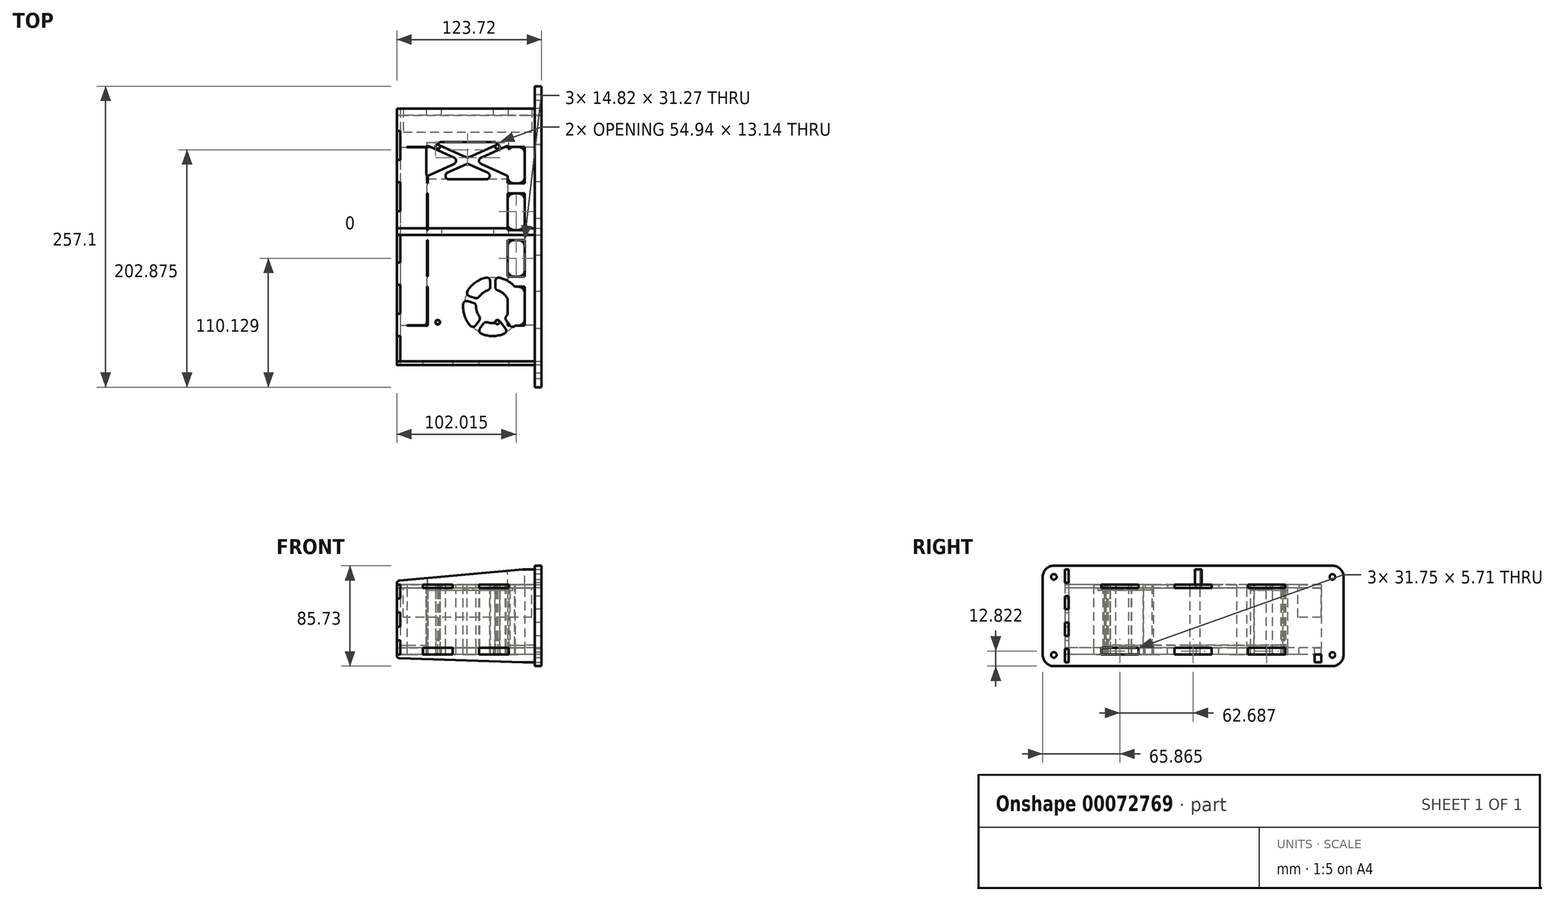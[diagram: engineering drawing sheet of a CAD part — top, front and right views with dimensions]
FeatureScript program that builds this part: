
annotation { "Feature Type Name" : "Feature", "Feature Type Description" : "" }
export const myFeature = defineFeature(function(context is Context, id is Id, definition is map)
    precondition{}
    {
        {
            assignVariable(context, id + "F0", {"name" : "duron_thin", "anyValue" : 3 * mm});
        }
        {
            assignVariable(context, id + "F1", {"name" : "duron_thick", "anyValue" : 5.7 * mm});
        }
        {
            var Q0;
            Q0=qCreatedBy(makeId("Top.planeOp"),FACE);
            var sketch = newSketch(context, id + "F2", { "sketchPlane" : qUnion([Q0])});
            skLineSegment(sketch, "E0.rect.bottom", {"start": v(57.5, 108) * mm, "end": v(-57.5, 108) * mm});
            skLineSegment(sketch, "E0.rect.top", {"start": v(57.5, -108) * mm, "end": v(-57.5, -108) * mm});
            skLineSegment(sketch, "E0.rect.left", {"start": v(57.5, 108) * mm, "end": v(57.5, -108) * mm});
            skLineSegment(sketch, "E0.rect.right", {"start": v(-57.5, 108) * mm, "end": v(-57.5, -108) * mm});
            skPoint(sketch, "E0.rect.middle", {"position": v(0, 0) * mm});
            skSolve(sketch);
        }
        {
            var Q0;
            Q0 = qSketchRegion(id + "F2", true);
            extrude(context, id + "F3", {"entities" : qUnion([Q0]), "depth" : 50 * mm + 1 * mm});
        }
        {
            var Q0;
            Q0=makeQuery(id+"F3.opExtrude","CAP_FACE",FACE,{"disambiguationData":[OSD([sQuery(id+"F2.wireOp",EDGE,"E0.rect.bottom"),sQuery(id+"F2.wireOp",EDGE,"E0.rect.top"),sQuery(id+"F2.wireOp",EDGE,"E0.rect.left"),sQuery(id+"F2.wireOp",EDGE,"E0.rect.right")])],"isStart":false});
            var sketch = newSketch(context, id + "F4", { "sketchPlane" : qUnion([Q0])});
            skCircle(sketch, "E1", {"center": v(21.5, -61) * mm, "radius": 24.5 * mm});
            skLineSegment(sketch, "E2.bottom", {"start": v(-55, 108) * mm, "end": v(55, 108) * mm});
            skLineSegment(sketch, "E2.top", {"start": v(-55, 88) * mm, "end": v(55, 88) * mm});
            skLineSegment(sketch, "E2.left", {"start": v(-55, 108) * mm, "end": v(-55, 88) * mm});
            skLineSegment(sketch, "E2.right", {"start": v(55, 108) * mm, "end": v(55, 88) * mm});
            skLineSegment(sketch, "E3.rect.bottom", {"start": v(-35, 79) * mm, "end": v(35, 79) * mm});
            skLineSegment(sketch, "E3.rect.top", {"start": v(-35, 48) * mm, "end": v(35, 48) * mm});
            skLineSegment(sketch, "E3.rect.left", {"start": v(-35, 79) * mm, "end": v(-35, 48) * mm});
            skLineSegment(sketch, "E3.rect.right", {"start": v(35, 79) * mm, "end": v(35, 48) * mm});
            skPoint(sketch, "E3.rect.middle", {"position": v(0, 63.5) * mm});
            skSolve(sketch);
        }
        {
            var Q0;
            Q0=makeQuery(id+"F4.imprint","IMPRINT",FACE,{"disambiguationData":[TD([[makeQuery(id+"F4.imprint","IMPRINT",EDGE,{"derivedFrom":sQuery(id+"F4.wireOp",EDGE,"E1")}),1.0]])]});
            var Q1;
            Q1=makeQuery(id+"F4.imprint","IMPRINT",FACE,{"disambiguationData":[TD([[makeQuery(id+"F4.imprint","IMPRINT",EDGE,{"derivedFrom":sQuery(id+"F4.wireOp",EDGE,"E3.rect.bottom")}),-1.0]])]});
            extrude(context, id + "F5", {"entities" : qUnion([Q0, Q1]), "operationType" : NewBodyOperationType.REMOVE, "oppositeDirection" : true, "depth" : 2 * mm});
        }
        {
            var Q0;
            Q0=makeQuery(id+"F4.imprint","IMPRINT",FACE,{"disambiguationData":[TD([[makeQuery(id+"F4.imprint","IMPRINT",EDGE,{"derivedFrom":sQuery(id+"F4.wireOp",EDGE,"E2.bottom")}),1.0]])]});
            extrude(context, id + "F6", {"entities" : qUnion([Q0]), "operationType" : NewBodyOperationType.REMOVE, "oppositeDirection" : true, "depth" : 25 * mm});
        }
        {
            var Q0;
            Q0=makeQuery(id+"F3.opExtrude","CAP_FACE",FACE,{"disambiguationData":[OSD([sQuery(id+"F2.wireOp",EDGE,"E0.rect.bottom"),sQuery(id+"F2.wireOp",EDGE,"E0.rect.top"),sQuery(id+"F2.wireOp",EDGE,"E0.rect.left"),sQuery(id+"F2.wireOp",EDGE,"E0.rect.right")])],"isStart":true});
            var sketch = newSketch(context, id + "F7", { "sketchPlane" : qUnion([Q0])});
            skLineSegment(sketch, "E4.bottom", {"start": v(57.5, 77) * mm, "end": v(34.5, 77) * mm});
            skLineSegment(sketch, "E4.top", {"start": v(57.5, -75) * mm, "end": v(34.5, -75) * mm});
            skLineSegment(sketch, "E4.left", {"start": v(57.5, 77) * mm, "end": v(57.5, -75) * mm});
            skLineSegment(sketch, "E4.right", {"start": v(34.5, 77) * mm, "end": v(34.5, -75) * mm});
            skLineSegment(sketch, "E5.bottom", {"start": v(-57.5, 77) * mm, "end": v(-34.5, 77) * mm});
            skLineSegment(sketch, "E5.top", {"start": v(-57.5, -75) * mm, "end": v(-34.5, -75) * mm});
            skLineSegment(sketch, "E5.left", {"start": v(-57.5, 77) * mm, "end": v(-57.5, -75) * mm});
            skLineSegment(sketch, "E5.right", {"start": v(-34.5, 77) * mm, "end": v(-34.5, -75) * mm});
            skPoint(sketch, "E6", {"position": v(48.25, -80) * mm});
            skPoint(sketch, "E7", {"position": v(48.25, 98.75) * mm});
            skPoint(sketch, "E8", {"position": v(-48.25, 98.75) * mm});
            skPoint(sketch, "E9", {"position": v(-48.25, -80) * mm});
            skPoint(sketch, "E10", {"position": v(-8, 10) * mm});
            skPoint(sketch, "E11", {"position": v(25.5, 74.5) * mm});
            skPoint(sketch, "E12", {"position": v(-25.5, 74.5) * mm});
            skPoint(sketch, "E13", {"position": v(25.5, -75.5) * mm});
            skPoint(sketch, "E14", {"position": v(-25.5, -75.5) * mm});
            skSolve(sketch);
        }
        {
            var Q0;
            Q0=makeQuery(id+"F7.imprint","IMPRINT",FACE,{"disambiguationData":[TD([[makeQuery(id+"F7.imprint","IMPRINT",EDGE,{"derivedFrom":sQuery(id+"F7.wireOp",EDGE,"E4.bottom")}),1.0]])]});
            var Q1;
            Q1=makeQuery(id+"F7.imprint","IMPRINT",FACE,{"disambiguationData":[TD([[makeQuery(id+"F7.imprint","IMPRINT",EDGE,{"derivedFrom":sQuery(id+"F7.wireOp",EDGE,"E5.bottom")}),-1.0]])]});
            extrude(context, id + "F8", {"entities" : qUnion([Q0, Q1]), "operationType" : NewBodyOperationType.REMOVE, "oppositeDirection" : true, "depth" : 2 * mm});
        }
        {
            var Q0;
            Q0=sQuery(id+"F7.wireOp",VERTEX,"E11");
            var Q1;
            Q1=sQuery(id+"F7.wireOp",VERTEX,"E12");
            var Q2;
            Q2=sQuery(id+"F7.wireOp",VERTEX,"E13");
            var Q3;
            Q3=sQuery(id+"F7.wireOp",VERTEX,"E14");
            var Q4;
            Q4=makeQuery(id+"F3.opExtrude","SWEPT_BODY",BODY,{"disambiguationData":[OSD([sQuery(id+"F2.wireOp",EDGE,"E0.rect.bottom"),sQuery(id+"F2.wireOp",EDGE,"E0.rect.top"),sQuery(id+"F2.wireOp",EDGE,"E0.rect.left"),sQuery(id+"F2.wireOp",EDGE,"E0.rect.right")])]});
            hole(context, id + "F9", {"style" : HoleStyle.SIMPLE, "holeDiameter" : 3.5 * mm, "endStyle" : HoleEndStyle.BLIND, "holeDepth" : 6.35 * mm, "locations" : qUnion([Q0, Q1, Q2, Q3]), "scope" : qUnion([Q4])});
        }
        {
            var Q0;
            Q0=makeQuery(id+"F3.opExtrude","SWEPT_FACE",FACE,{"disambiguationData":[OSD([sQuery(id+"F2.wireOp",EDGE,"E0.rect.left")])]});
            var sketch = newSketch(context, id + "F10", { "sketchPlane" : qUnion([Q0])});
            skLineSegment(sketch, "E15.bottom", {"start": v(-130.05, 70.05) * mm, "end": v(127.05, 70.05) * mm});
            skLineSegment(sketch, "E15.top", {"start": v(-130.05, -15.67) * mm, "end": v(127.05, -15.67) * mm});
            skLineSegment(sketch, "E15.left", {"start": v(-130.05, 70.05) * mm, "end": v(-130.05, -15.68) * mm});
            skLineSegment(sketch, "E15.right", {"start": v(127.05, 70.05) * mm, "end": v(127.05, -15.67) * mm});
            skSolve(sketch);
        }
        {
            var Q0;
            Q0 = qSketchRegion(id + "F10", true);
            extrude(context, id + "F11", {"entities" : qUnion([Q0]), "depth" : getVariable(context, 'duron_thick')});
        }
        {
            var Q0;
            Q0=makeQuery(id+"F3.opExtrude","SWEPT_FACE",FACE,{"disambiguationData":[OSD([sQuery(id+"F2.wireOp",EDGE,"E0.rect.top")])]});
            var sketch = newSketch(context, id + "F12", { "sketchPlane" : qUnion([Q0])});
            skLineSegment(sketch, "E16.0.1", {"start": v(57.5, -15.68) * mm, "end": v(63.21, -15.68) * mm, "construction": true});
            skLineSegment(sketch, "E16.0.2", {"start": v(63.21, -12.5) * mm, "end": v(63.21, 66.88) * mm});
            skLineSegment(sketch, "E16.0.3", {"start": v(63.21, 70.05) * mm, "end": v(57.5, 70.05) * mm, "construction": true});
            skLineSegment(sketch, "E17.0.0", {"start": v(-57.5, 0) * mm, "end": v(57.5, 0) * mm, "construction": true});
            skLineSegment(sketch, "E17.0.2", {"start": v(57.5, 51) * mm, "end": v(-57.5, 51) * mm, "construction": true});
            skLineSegment(sketch, "E17.0.3", {"start": v(-57.5, 51) * mm, "end": v(-57.5, 0) * mm, "construction": true});
            skLineSegment(sketch, "E18", {"start": v(-60.5, 57.17) * mm, "end": v(-60.5, -8.89) * mm});
            skLineSegment(sketch, "E19", {"start": v(47.34, 66.88) * mm, "end": v(-60.5, 57.17) * mm});
            skLineSegment(sketch, "E20", {"start": v(-60.5, -8.9) * mm, "end": v(47.34, -12.5) * mm});
            skLineSegment(sketch, "E21", {"start": v(47.34, -12.5) * mm, "end": v(63.21, -12.5) * mm});
            skLineSegment(sketch, "E22", {"start": v(47.34, 66.88) * mm, "end": v(63.21, 66.88) * mm});
            skLineSegment(sketch, "E23.bottom", {"start": v(63.21, 55.54) * mm, "end": v(57.5, 55.54) * mm});
            skLineSegment(sketch, "E23.top", {"start": v(63.21, 44.2) * mm, "end": v(57.5, 44.2) * mm});
            skLineSegment(sketch, "E23.left", {"start": v(63.21, 55.54) * mm, "end": v(63.21, 44.2) * mm});
            skLineSegment(sketch, "E23.right", {"start": v(57.5, 55.54) * mm, "end": v(57.5, 44.2) * mm});
            skLineSegment(sketch, "E24.bottom", {"start": v(63.21, 32.86) * mm, "end": v(57.5, 32.86) * mm});
            skLineSegment(sketch, "E24.top", {"start": v(63.21, 21.52) * mm, "end": v(57.5, 21.52) * mm});
            skLineSegment(sketch, "E24.left", {"start": v(63.21, 32.86) * mm, "end": v(63.21, 21.52) * mm});
            skLineSegment(sketch, "E24.right", {"start": v(57.5, 32.86) * mm, "end": v(57.5, 21.52) * mm});
            skLineSegment(sketch, "E25.bottom", {"start": v(63.21, 10.18) * mm, "end": v(57.5, 10.18) * mm});
            skLineSegment(sketch, "E25.top", {"start": v(63.21, -1.16) * mm, "end": v(57.5, -1.16) * mm});
            skLineSegment(sketch, "E25.left", {"start": v(63.21, 10.18) * mm, "end": v(63.21, -1.16) * mm});
            skLineSegment(sketch, "E25.right", {"start": v(57.5, 10.18) * mm, "end": v(57.5, -1.16) * mm});
            skLineSegment(sketch, "E26", {"start": v(57.5, 44.2) * mm, "end": v(57.5, 32.86) * mm, "construction": true});
            skLineSegment(sketch, "E27", {"start": v(57.5, 21.52) * mm, "end": v(57.5, 10.18) * mm, "construction": true});
            skLineSegment(sketch, "E28", {"start": v(57.5, -1.16) * mm, "end": v(57.5, -12.5) * mm, "construction": true});
            skLineSegment(sketch, "E29", {"start": v(57.5, 55.54) * mm, "end": v(57.5, 66.88) * mm, "construction": true});
            skSolve(sketch);
        }
        {
            var Q0;
            Q0=makeQuery(id+"F12.imprint","IMPRINT",FACE,{"disambiguationData":[TD([[makeQuery(id+"F12.imprint","IMPRINT",EDGE,{"derivedFrom":sQuery(id+"F12.wireOp",EDGE,"E18")}),1.0]])]});
            var Q1;
            {var subQ6=sQuery(id+"F12.wireOp",EDGE,"E24.right");Q1=makeQuery(id+"F12.imprint","IMPRINT",FACE,{"disambiguationData":[TD([[makeQuery(id+"F12.imprint","IMPRINT",EDGE,{"derivedFrom":subQ6}),-1.0]])]});}
            var Q2;
            {var subQ0=sQuery(id+"F12.wireOp",EDGE,"E23.top");Q2=makeQuery(id+"F12.imprint","IMPRINT",FACE,{"disambiguationData":[TD([[makeQuery(id+"F12.imprint","IMPRINT",EDGE,{"derivedFrom":subQ0}),1.0]])]});}
            var Q3;
            {var subQ0=sQuery(id+"F12.wireOp",EDGE,"E24.top");Q3=makeQuery(id+"F12.imprint","IMPRINT",FACE,{"disambiguationData":[TD([[makeQuery(id+"F12.imprint","IMPRINT",EDGE,{"derivedFrom":subQ0}),1.0]])]});}
            extrude(context, id + "F13", {"entities" : qUnion([Q0, Q1, Q2, Q3]), "depth" : getVariable(context, 'duron_thin')});
        }
        {
            var Q0;
            Q0=makeQuery(id+"F3.opExtrude","CAP_FACE",FACE,{"disambiguationData":[OSD([sQuery(id+"F2.wireOp",EDGE,"E0.rect.bottom"),sQuery(id+"F2.wireOp",EDGE,"E0.rect.top"),sQuery(id+"F2.wireOp",EDGE,"E0.rect.left"),sQuery(id+"F2.wireOp",EDGE,"E0.rect.right")])],"isStart":true});
            var sketch = newSketch(context, id + "F14", { "sketchPlane" : qUnion([Q0])});
            skLineSegment(sketch, "E30.bottom", {"start": v(63.22, -108) * mm, "end": v(57.5, -108) * mm, "construction": true});
            skLineSegment(sketch, "E30.top", {"start": v(63.21, 111) * mm, "end": v(57.5, 111) * mm});
            skLineSegment(sketch, "E30.left", {"start": v(63.22, -77.06) * mm, "end": v(63.22, -45.31) * mm});
            skLineSegment(sketch, "E30.right", {"start": v(-60.5, -108) * mm, "end": v(-60.5, 111) * mm});
            skLineSegment(sketch, "E31.bottom", {"start": v(63.21, 80.06) * mm, "end": v(57.5, 80.06) * mm});
            skLineSegment(sketch, "E31.top", {"start": v(63.21, 48.31) * mm, "end": v(57.5, 48.31) * mm});
            skLineSegment(sketch, "E31.left", {"start": v(63.21, 80.06) * mm, "end": v(63.21, 48.31) * mm});
            skLineSegment(sketch, "E31.right", {"start": v(57.5, 80.06) * mm, "end": v(57.5, 48.31) * mm, "construction": true});
            skLineSegment(sketch, "E32.bottom", {"start": v(63.21, 17.37) * mm, "end": v(57.5, 17.37) * mm});
            skLineSegment(sketch, "E32.top", {"start": v(63.21, -14.38) * mm, "end": v(57.5, -14.38) * mm});
            skLineSegment(sketch, "E32.left", {"start": v(63.21, 17.37) * mm, "end": v(63.21, -14.38) * mm});
            skLineSegment(sketch, "E32.right", {"start": v(57.5, 17.37) * mm, "end": v(57.5, -14.38) * mm, "construction": true});
            skLineSegment(sketch, "E33.bottom", {"start": v(63.21, -45.31) * mm, "end": v(57.5, -45.31) * mm});
            skLineSegment(sketch, "E33.top", {"start": v(63.21, -77.06) * mm, "end": v(57.5, -77.06) * mm});
            skLineSegment(sketch, "E33.left", {"start": v(63.21, -45.31) * mm, "end": v(63.21, -77.06) * mm});
            skLineSegment(sketch, "E33.right", {"start": v(57.5, -45.31) * mm, "end": v(57.5, -77.06) * mm, "construction": true});
            skLineSegment(sketch, "E34", {"start": v(57.5, -45.31) * mm, "end": v(57.5, -14.38) * mm});
            skLineSegment(sketch, "E35", {"start": v(57.5, 17.37) * mm, "end": v(57.5, 48.31) * mm});
            skLineSegment(sketch, "E36", {"start": v(57.5, 80.06) * mm, "end": v(57.5, 111) * mm});
            skLineSegment(sketch, "E37", {"start": v(57.5, -77.06) * mm, "end": v(57.5, -108) * mm});
            skLineSegment(sketch, "E38.trimOffspring", {"start": v(63.21, -14.38) * mm, "end": v(63.21, 17.37) * mm});
            skLineSegment(sketch, "E39.trimOffspring", {"start": v(63.21, 48.31) * mm, "end": v(63.21, 80.06) * mm});
            skLineSegment(sketch, "E40.top", {"start": v(35.1, 111) * mm, "end": v(9.7, 111) * mm});
            skLineSegment(sketch, "E40.left", {"start": v(35.1, 108) * mm, "end": v(35.1, 111) * mm});
            skLineSegment(sketch, "E40.right", {"start": v(9.7, 108) * mm, "end": v(9.7, 111) * mm});
            skLineSegment(sketch, "E41.top", {"start": v(-12.7, 111) * mm, "end": v(-38.1, 111) * mm});
            skLineSegment(sketch, "E41.left", {"start": v(-12.7, 108) * mm, "end": v(-12.7, 111) * mm});
            skLineSegment(sketch, "E41.right", {"start": v(-38.1, 108) * mm, "end": v(-38.1, 111) * mm});
            skLineSegment(sketch, "E42", {"start": v(9.7, 111) * mm, "end": v(-12.7, 111) * mm, "construction": true});
            skLineSegment(sketch, "E43", {"start": v(-38.1, 111) * mm, "end": v(-60.5, 111) * mm, "construction": true});
            skLineSegment(sketch, "E44", {"start": v(35.1, 111) * mm, "end": v(57.5, 111) * mm, "construction": true});
            skLineSegment(sketch, "E45", {"start": v(-38.1, 108) * mm, "end": v(-60.5, 108) * mm});
            skLineSegment(sketch, "E46", {"start": v(-12.7, 108) * mm, "end": v(9.7, 108) * mm});
            skLineSegment(sketch, "E47", {"start": v(35.1, 108) * mm, "end": v(57.5, 108) * mm});
            skLineSegment(sketch, "E48", {"start": v(57.5, -108) * mm, "end": v(-60.5, -108) * mm});
            skSolve(sketch);
        }
        {
            var Q0;
            {var subQ0=sQuery(id+"F7.wireOp",EDGE,"E5.bottom");Q0=makeQuery(id+"F14.imprint","IMPRINT",FACE,{"disambiguationData":[TD([[makeQuery(id+"F14.imprint","IMPRINT",EDGE,{"derivedFrom":makeQuery(id+"F8.boolean.opBoolean","COPY",EDGE,{"derivedFrom":makeQuery(id+"F8.opExtrude","CAP_EDGE",EDGE,{"disambiguationData":[OSD([subQ0])],"isStart":true})})}),-1.0]])]});}
            var Q1;
            {var subQ11=sQuery(id+"F14.wireOp",EDGE,"E37");Q1=makeQuery(id+"F14.imprint","IMPRINT",FACE,{"disambiguationData":[TD([[makeQuery(id+"F14.imprint","IMPRINT",EDGE,{"derivedFrom":subQ11}),1.0]])]});}
            var Q2;
            {var subQ0=sQuery(id+"F14.wireOp",EDGE,"E40.left");Q2=makeQuery(id+"F14.imprint","IMPRINT",FACE,{"disambiguationData":[TD([[makeQuery(id+"F14.imprint","IMPRINT",EDGE,{"derivedFrom":subQ0}),1.0]])]});}
            var Q3;
            {var subQ0=sQuery(id+"F14.wireOp",EDGE,"E41.left");Q3=makeQuery(id+"F14.imprint","IMPRINT",FACE,{"disambiguationData":[TD([[makeQuery(id+"F14.imprint","IMPRINT",EDGE,{"derivedFrom":subQ0}),1.0]])]});}
            var Q4;
            Q4=makeQuery(id+"F14.imprint","IMPRINT",FACE,{"disambiguationData":[TD([[makeQuery(id+"F14.imprint","IMPRINT",EDGE,{"derivedFrom":makeQuery(id+"F9.hole-1.boolean.opBoolean","COPY",EDGE,{"derivedFrom":makeQuery(id+"F9.hole-1.opRevolve","SWEPT_EDGE",EDGE,{"disambiguationData":[OSD([sQuery(id+"F9.hole-1.sketch.wireOp",EDGE,"core_line_2"),sQuery(id+"F9.hole-1.sketch.wireOp",EDGE,"core_line_3")])]})})}),1.0]])]});
            var Q5;
            Q5=makeQuery(id+"F14.imprint","IMPRINT",FACE,{"disambiguationData":[TD([[makeQuery(id+"F14.imprint","IMPRINT",EDGE,{"derivedFrom":makeQuery(id+"F9.hole-3.boolean.opBoolean","COPY",EDGE,{"derivedFrom":makeQuery(id+"F9.hole-3.opRevolve","SWEPT_EDGE",EDGE,{"disambiguationData":[OSD([sQuery(id+"F9.hole-3.sketch.wireOp",EDGE,"core_line_2"),sQuery(id+"F9.hole-3.sketch.wireOp",EDGE,"core_line_3")])]})})}),1.0]])]});
            var Q6;
            Q6=makeQuery(id+"F14.imprint","IMPRINT",FACE,{"disambiguationData":[TD([[makeQuery(id+"F14.imprint","IMPRINT",EDGE,{"derivedFrom":makeQuery(id+"F9.hole-0.boolean.opBoolean","COPY",EDGE,{"derivedFrom":makeQuery(id+"F9.hole-0.opRevolve","SWEPT_EDGE",EDGE,{"disambiguationData":[OSD([sQuery(id+"F9.hole-0.sketch.wireOp",EDGE,"core_line_2"),sQuery(id+"F9.hole-0.sketch.wireOp",EDGE,"core_line_3")])]})})}),1.0]])]});
            var Q7;
            Q7=makeQuery(id+"F14.imprint","IMPRINT",FACE,{"disambiguationData":[TD([[makeQuery(id+"F14.imprint","IMPRINT",EDGE,{"derivedFrom":makeQuery(id+"F9.hole-2.boolean.opBoolean","COPY",EDGE,{"derivedFrom":makeQuery(id+"F9.hole-2.opRevolve","SWEPT_EDGE",EDGE,{"disambiguationData":[OSD([sQuery(id+"F9.hole-2.sketch.wireOp",EDGE,"core_line_2"),sQuery(id+"F9.hole-2.sketch.wireOp",EDGE,"core_line_3")])]})})}),1.0]])]});
            var Q8;
            {var subQ10=sQuery(id+"F14.wireOp",EDGE,"E31.bottom");Q8=makeQuery(id+"F14.imprint","IMPRINT",FACE,{"disambiguationData":[TD([[makeQuery(id+"F14.imprint","IMPRINT",EDGE,{"derivedFrom":subQ10}),1.0]])]});}
            extrude(context, id + "F15", {"entities" : qUnion([Q0, Q1, Q2, Q3, Q4, Q5, Q6, Q7, Q8]), "depth" : getVariable(context, 'duron_thick')});
        }
        {
            var Q0;
            Q0=makeQuery(id+"F3.opExtrude","CAP_FACE",FACE,{"disambiguationData":[OSD([sQuery(id+"F2.wireOp",EDGE,"E0.rect.bottom"),sQuery(id+"F2.wireOp",EDGE,"E0.rect.top"),sQuery(id+"F2.wireOp",EDGE,"E0.rect.left"),sQuery(id+"F2.wireOp",EDGE,"E0.rect.right")])],"isStart":false});
            var sketch = newSketch(context, id + "F16", { "sketchPlane" : qUnion([Q0])});
            skLineSegment(sketch, "E49.0.0", {"start": v(-60.5, 108) * mm, "end": v(57.5, 108) * mm});
            skLineSegment(sketch, "E49.0.1", {"start": v(57.5, 108) * mm, "end": v(57.5, 77.06) * mm});
            skLineSegment(sketch, "E49.0.2", {"start": v(57.5, 77.06) * mm, "end": v(63.21, 77.06) * mm});
            skLineSegment(sketch, "E49.0.3", {"start": v(63.21, 77.06) * mm, "end": v(63.21, 45.31) * mm});
            skLineSegment(sketch, "E49.0.4", {"start": v(63.21, 45.31) * mm, "end": v(57.5, 45.31) * mm});
            skLineSegment(sketch, "E49.0.5", {"start": v(57.5, 45.31) * mm, "end": v(57.5, 14.38) * mm});
            skLineSegment(sketch, "E49.0.6", {"start": v(57.5, 14.38) * mm, "end": v(63.21, 14.38) * mm});
            skLineSegment(sketch, "E49.0.7", {"start": v(63.21, 14.38) * mm, "end": v(63.21, -17.37) * mm});
            skLineSegment(sketch, "E49.0.8", {"start": v(63.21, -17.37) * mm, "end": v(57.5, -17.37) * mm});
            skLineSegment(sketch, "E49.0.9", {"start": v(57.5, -17.37) * mm, "end": v(57.5, -48.31) * mm});
            skLineSegment(sketch, "E49.0.10", {"start": v(57.5, -48.31) * mm, "end": v(63.21, -48.31) * mm});
            skLineSegment(sketch, "E49.0.11", {"start": v(63.21, -48.31) * mm, "end": v(63.21, -80.06) * mm});
            skLineSegment(sketch, "E49.0.12", {"start": v(63.21, -80.06) * mm, "end": v(57.5, -80.06) * mm});
            skLineSegment(sketch, "E49.0.13", {"start": v(57.5, -80.06) * mm, "end": v(57.5, -108) * mm});
            skLineSegment(sketch, "E49.0.14", {"start": v(57.5, -108) * mm, "end": v(35.1, -108) * mm});
            skLineSegment(sketch, "E49.0.15", {"start": v(35.1, -108) * mm, "end": v(35.1, -111) * mm});
            skLineSegment(sketch, "E49.0.16", {"start": v(35.1, -111) * mm, "end": v(9.7, -111) * mm});
            skLineSegment(sketch, "E49.0.17", {"start": v(9.7, -111) * mm, "end": v(9.7, -108) * mm});
            skLineSegment(sketch, "E49.0.18", {"start": v(9.7, -108) * mm, "end": v(-12.7, -108) * mm});
            skLineSegment(sketch, "E49.0.19", {"start": v(-12.7, -108) * mm, "end": v(-12.7, -111) * mm});
            skLineSegment(sketch, "E49.0.20", {"start": v(-12.7, -111) * mm, "end": v(-38.1, -111) * mm});
            skLineSegment(sketch, "E49.0.21", {"start": v(-38.1, -111) * mm, "end": v(-38.1, -108) * mm});
            skLineSegment(sketch, "E49.0.22", {"start": v(-38.1, -108) * mm, "end": v(-60.5, -108) * mm});
            skLineSegment(sketch, "E49.0.23", {"start": v(-60.5, -108) * mm, "end": v(-60.5, 108) * mm});
            skSolve(sketch);
        }
        {
            var Q0;
            Q0 = qSketchRegion(id + "F16", true);
            extrude(context, id + "F17", {"entities" : qUnion([Q0]), "depth" : getVariable(context, 'duron_thin')});
        }
        {
            var Q0;
            Q0=makeQuery(id+"F3.opExtrude","SWEPT_FACE",FACE,{"disambiguationData":[OSD([sQuery(id+"F2.wireOp",EDGE,"E0.rect.right")])]});
            var sketch = newSketch(context, id + "F18", { "sketchPlane" : qUnion([Q0])});
            skLineSegment(sketch, "E50.bottom", {"start": v(-88.95, 54) * mm, "end": v(-64.2, 54) * mm});
            skLineSegment(sketch, "E50.top", {"start": v(-88.95, -5.72) * mm, "end": v(-64.2, -5.72) * mm});
            skLineSegment(sketch, "E50.left", {"start": v(-108, 54) * mm, "end": v(-108, -5.72) * mm});
            skLineSegment(sketch, "E50.right", {"start": v(111, 54) * mm, "end": v(111, 42.05) * mm});
            skLineSegment(sketch, "E51.bottom", {"start": v(111, 42.05) * mm, "end": v(108, 42.05) * mm});
            skLineSegment(sketch, "E51.top", {"start": v(111, 30.11) * mm, "end": v(108, 30.11) * mm});
            skLineSegment(sketch, "E51.right", {"start": v(108, 42.05) * mm, "end": v(108, 30.11) * mm});
            skLineSegment(sketch, "E52.bottom", {"start": v(111, 18.17) * mm, "end": v(108, 18.17) * mm});
            skLineSegment(sketch, "E52.top", {"start": v(111, 6.23) * mm, "end": v(108, 6.23) * mm});
            skLineSegment(sketch, "E52.right", {"start": v(108, 18.17) * mm, "end": v(108, 6.23) * mm});
            skLineSegment(sketch, "E53", {"start": v(108, 18.17) * mm, "end": v(108, 30.11) * mm, "construction": true});
            skLineSegment(sketch, "E54", {"start": v(108, 42.05) * mm, "end": v(108, 54) * mm, "construction": true});
            skLineSegment(sketch, "E55", {"start": v(108, 6.23) * mm, "end": v(108, -5.72) * mm, "construction": true});
            skLineSegment(sketch, "E56.trimOffspring", {"start": v(111, 30.11) * mm, "end": v(111, 18.17) * mm});
            skLineSegment(sketch, "E57.trimOffspring", {"start": v(111, 6.23) * mm, "end": v(111, -5.72) * mm});
            skLineSegment(sketch, "E58.top", {"start": v(-108, 51) * mm, "end": v(-88.95, 51) * mm});
            skLineSegment(sketch, "E58.left", {"start": v(-108, 54) * mm, "end": v(-108, 51) * mm});
            skLineSegment(sketch, "E58.right", {"start": v(-88.95, 54) * mm, "end": v(-88.95, 51) * mm});
            skLineSegment(sketch, "E59.top", {"start": v(-64.2, 51) * mm, "end": v(-45.15, 51) * mm});
            skLineSegment(sketch, "E59.left", {"start": v(-64.2, 54) * mm, "end": v(-64.2, 51) * mm});
            skLineSegment(sketch, "E59.right", {"start": v(-45.15, 54) * mm, "end": v(-45.15, 51) * mm});
            skLineSegment(sketch, "E60.top", {"start": v(-20.4, 51) * mm, "end": v(-1.35, 51) * mm});
            skLineSegment(sketch, "E60.left", {"start": v(-20.4, 54) * mm, "end": v(-20.4, 51) * mm});
            skLineSegment(sketch, "E60.right", {"start": v(-1.35, 54) * mm, "end": v(-1.35, 51) * mm});
            skLineSegment(sketch, "E61.top", {"start": v(23.4, 51) * mm, "end": v(42.45, 51) * mm});
            skLineSegment(sketch, "E61.left", {"start": v(23.4, 54) * mm, "end": v(23.4, 51) * mm});
            skLineSegment(sketch, "E61.right", {"start": v(42.45, 54) * mm, "end": v(42.45, 51) * mm});
            skLineSegment(sketch, "E62.top", {"start": v(67.2, 51) * mm, "end": v(86.25, 51) * mm});
            skLineSegment(sketch, "E62.left", {"start": v(67.2, 54) * mm, "end": v(67.2, 51) * mm});
            skLineSegment(sketch, "E62.right", {"start": v(86.25, 54) * mm, "end": v(86.25, 51) * mm});
            skLineSegment(sketch, "E63.top", {"start": v(-108, 0) * mm, "end": v(-88.95, 0) * mm});
            skLineSegment(sketch, "E63.left", {"start": v(-108, -5.72) * mm, "end": v(-108, 0) * mm});
            skLineSegment(sketch, "E63.right", {"start": v(-88.95, -5.72) * mm, "end": v(-88.95, 0) * mm});
            skLineSegment(sketch, "E64.top", {"start": v(-64.2, 0) * mm, "end": v(-45.15, 0) * mm});
            skLineSegment(sketch, "E64.left", {"start": v(-64.2, -5.72) * mm, "end": v(-64.2, 0) * mm});
            skLineSegment(sketch, "E64.right", {"start": v(-45.15, -5.72) * mm, "end": v(-45.15, 0) * mm});
            skLineSegment(sketch, "E65.top", {"start": v(-20.4, 0) * mm, "end": v(-1.35, 0) * mm});
            skLineSegment(sketch, "E65.left", {"start": v(-20.4, -5.72) * mm, "end": v(-20.4, 0) * mm});
            skLineSegment(sketch, "E65.right", {"start": v(-1.35, -5.72) * mm, "end": v(-1.35, 0) * mm});
            skLineSegment(sketch, "E66.top", {"start": v(23.4, 0) * mm, "end": v(42.45, 0) * mm});
            skLineSegment(sketch, "E66.left", {"start": v(23.4, -5.71) * mm, "end": v(23.4, 0) * mm});
            skLineSegment(sketch, "E66.right", {"start": v(42.45, -5.71) * mm, "end": v(42.45, 0) * mm});
            skLineSegment(sketch, "E67.top", {"start": v(67.2, 0) * mm, "end": v(86.25, 0) * mm});
            skLineSegment(sketch, "E67.left", {"start": v(67.2, -5.71) * mm, "end": v(67.2, 0) * mm});
            skLineSegment(sketch, "E67.right", {"start": v(86.25, -5.71) * mm, "end": v(86.25, 0) * mm});
            skLineSegment(sketch, "E68", {"start": v(-88.95, 51) * mm, "end": v(-64.2, 51) * mm, "construction": true});
            skLineSegment(sketch, "E69", {"start": v(-45.15, 51) * mm, "end": v(-20.4, 51) * mm, "construction": true});
            skLineSegment(sketch, "E70", {"start": v(-1.35, 51) * mm, "end": v(23.4, 51) * mm, "construction": true});
            skLineSegment(sketch, "E71", {"start": v(42.45, 51) * mm, "end": v(67.2, 51) * mm, "construction": true});
            skLineSegment(sketch, "E72", {"start": v(86.25, 51) * mm, "end": v(111, 51) * mm, "construction": true});
            skLineSegment(sketch, "E73.trimOffspring", {"start": v(-45.15, 54) * mm, "end": v(-20.4, 54) * mm});
            skLineSegment(sketch, "E74.trimOffspring", {"start": v(-1.35, 54) * mm, "end": v(23.4, 54) * mm});
            skLineSegment(sketch, "E75.trimOffspring", {"start": v(42.45, 54) * mm, "end": v(67.2, 54) * mm});
            skLineSegment(sketch, "E76.trimOffspring", {"start": v(86.25, 54) * mm, "end": v(111, 54) * mm});
            skLineSegment(sketch, "E77.trimOffspring", {"start": v(86.25, -5.72) * mm, "end": v(111, -5.72) * mm});
            skLineSegment(sketch, "E78.trimOffspring", {"start": v(42.45, -5.72) * mm, "end": v(67.2, -5.72) * mm});
            skLineSegment(sketch, "E79.trimOffspring", {"start": v(-1.35, -5.72) * mm, "end": v(23.4, -5.72) * mm});
            skLineSegment(sketch, "E80.trimOffspring", {"start": v(-45.15, -5.72) * mm, "end": v(-20.4, -5.72) * mm});
            skSolve(sketch);
        }
        {
            var Q0;
            Q0 = qSketchRegion(id + "F18", true);
            extrude(context, id + "F19", {"entities" : qUnion([Q0]), "depth" : getVariable(context, 'duron_thin')});
        }
        {
            var Q0;
            Q0=makeQuery(id+"F19.opExtrude","SWEPT_BODY",BODY,{"disambiguationData":[OSD([sQuery(id+"F18.wireOp",EDGE,"E50.bottom"),sQuery(id+"F18.wireOp",EDGE,"E50.top"),sQuery(id+"F18.wireOp",EDGE,"E50.left"),sQuery(id+"F18.wireOp",EDGE,"E50.right"),sQuery(id+"F18.wireOp",EDGE,"E51.bottom"),sQuery(id+"F18.wireOp",EDGE,"E51.top"),sQuery(id+"F18.wireOp",EDGE,"E51.right"),sQuery(id+"F18.wireOp",EDGE,"E52.bottom"),sQuery(id+"F18.wireOp",EDGE,"E52.top"),sQuery(id+"F18.wireOp",EDGE,"E52.right"),sQuery(id+"F18.wireOp",EDGE,"E56.trimOffspring"),sQuery(id+"F18.wireOp",EDGE,"E57.trimOffspring"),sQuery(id+"F18.wireOp",EDGE,"E58.top"),sQuery(id+"F18.wireOp",EDGE,"E58.right"),sQuery(id+"F18.wireOp",EDGE,"E59.top"),sQuery(id+"F18.wireOp",EDGE,"E59.left"),sQuery(id+"F18.wireOp",EDGE,"E59.right"),sQuery(id+"F18.wireOp",EDGE,"E60.top"),sQuery(id+"F18.wireOp",EDGE,"E60.left"),sQuery(id+"F18.wireOp",EDGE,"E60.right"),sQuery(id+"F18.wireOp",EDGE,"E61.top"),sQuery(id+"F18.wireOp",EDGE,"E61.left"),sQuery(id+"F18.wireOp",EDGE,"E61.right"),sQuery(id+"F18.wireOp",EDGE,"E62.top"),sQuery(id+"F18.wireOp",EDGE,"E62.left"),sQuery(id+"F18.wireOp",EDGE,"E62.right"),sQuery(id+"F18.wireOp",EDGE,"E63.top"),sQuery(id+"F18.wireOp",EDGE,"E63.right"),sQuery(id+"F18.wireOp",EDGE,"E64.top"),sQuery(id+"F18.wireOp",EDGE,"E64.left"),sQuery(id+"F18.wireOp",EDGE,"E64.right"),sQuery(id+"F18.wireOp",EDGE,"E65.top"),sQuery(id+"F18.wireOp",EDGE,"E65.left"),sQuery(id+"F18.wireOp",EDGE,"E65.right"),sQuery(id+"F18.wireOp",EDGE,"E66.top"),sQuery(id+"F18.wireOp",EDGE,"E66.left"),sQuery(id+"F18.wireOp",EDGE,"E66.right"),sQuery(id+"F18.wireOp",EDGE,"E67.top"),sQuery(id+"F18.wireOp",EDGE,"E67.left"),sQuery(id+"F18.wireOp",EDGE,"E67.right"),sQuery(id+"F18.wireOp",EDGE,"E73.trimOffspring"),sQuery(id+"F18.wireOp",EDGE,"E74.trimOffspring"),sQuery(id+"F18.wireOp",EDGE,"E75.trimOffspring"),sQuery(id+"F18.wireOp",EDGE,"E76.trimOffspring"),sQuery(id+"F18.wireOp",EDGE,"E77.trimOffspring"),sQuery(id+"F18.wireOp",EDGE,"E78.trimOffspring"),sQuery(id+"F18.wireOp",EDGE,"E79.trimOffspring"),sQuery(id+"F18.wireOp",EDGE,"E80.trimOffspring")])]});
            var Q1;
            Q1=makeQuery(id+"F17.opExtrude","SWEPT_BODY",BODY,{"disambiguationData":[OSD([sQuery(id+"F16.wireOp",EDGE,"E49.0.0"),sQuery(id+"F16.wireOp",EDGE,"E49.0.1"),sQuery(id+"F16.wireOp",EDGE,"E49.0.2"),sQuery(id+"F16.wireOp",EDGE,"E49.0.3"),sQuery(id+"F16.wireOp",EDGE,"E49.0.4"),sQuery(id+"F16.wireOp",EDGE,"E49.0.5"),sQuery(id+"F16.wireOp",EDGE,"E49.0.6"),sQuery(id+"F16.wireOp",EDGE,"E49.0.7"),sQuery(id+"F16.wireOp",EDGE,"E49.0.8"),sQuery(id+"F16.wireOp",EDGE,"E49.0.9"),sQuery(id+"F16.wireOp",EDGE,"E49.0.10"),sQuery(id+"F16.wireOp",EDGE,"E49.0.11"),sQuery(id+"F16.wireOp",EDGE,"E49.0.12"),sQuery(id+"F16.wireOp",EDGE,"E49.0.13"),sQuery(id+"F16.wireOp",EDGE,"E49.0.14"),sQuery(id+"F16.wireOp",EDGE,"E49.0.15"),sQuery(id+"F16.wireOp",EDGE,"E49.0.16"),sQuery(id+"F16.wireOp",EDGE,"E49.0.17"),sQuery(id+"F16.wireOp",EDGE,"E49.0.18"),sQuery(id+"F16.wireOp",EDGE,"E49.0.19"),sQuery(id+"F16.wireOp",EDGE,"E49.0.20"),sQuery(id+"F16.wireOp",EDGE,"E49.0.21"),sQuery(id+"F16.wireOp",EDGE,"E49.0.22"),sQuery(id+"F16.wireOp",EDGE,"E49.0.23")])]});
            var Q2;
            Q2=makeQuery(id+"F15.opExtrude","SWEPT_BODY",BODY,{"disambiguationData":[OSD([sQuery(id+"F14.wireOp",EDGE,"E30.right"),sQuery(id+"F14.wireOp",EDGE,"E31.bottom"),sQuery(id+"F14.wireOp",EDGE,"E31.top"),sQuery(id+"F14.wireOp",EDGE,"E32.bottom"),sQuery(id+"F14.wireOp",EDGE,"E32.top"),sQuery(id+"F14.wireOp",EDGE,"E33.bottom"),sQuery(id+"F14.wireOp",EDGE,"E33.top"),sQuery(id+"F14.wireOp",EDGE,"E33.left"),sQuery(id+"F14.wireOp",EDGE,"E34"),sQuery(id+"F14.wireOp",EDGE,"E35"),sQuery(id+"F14.wireOp",EDGE,"E36"),sQuery(id+"F14.wireOp",EDGE,"E37"),sQuery(id+"F14.wireOp",EDGE,"E38.trimOffspring"),sQuery(id+"F14.wireOp",EDGE,"E39.trimOffspring"),sQuery(id+"F14.wireOp",EDGE,"E40.left"),sQuery(id+"F14.wireOp",EDGE,"E40.right"),sQuery(id+"F14.wireOp",EDGE,"E41.left"),sQuery(id+"F14.wireOp",EDGE,"E41.right"),sQuery(id+"F14.wireOp",EDGE,"E40.top"),sQuery(id+"F14.wireOp",EDGE,"E41.top"),sQuery(id+"F14.wireOp",EDGE,"E45"),sQuery(id+"F14.wireOp",EDGE,"E46"),sQuery(id+"F14.wireOp",EDGE,"E47"),sQuery(id+"F14.wireOp",EDGE,"E48")])]});
            var Q3;
            Q3=makeQuery(id+"F11.opExtrude","SWEPT_BODY",BODY,{"disambiguationData":[OSD([sQuery(id+"F10.wireOp",EDGE,"E15.bottom"),sQuery(id+"F10.wireOp",EDGE,"E15.top"),sQuery(id+"F10.wireOp",EDGE,"E15.left"),sQuery(id+"F10.wireOp",EDGE,"E15.right")])]});
            booleanBodies(context, id + "F20", {"operationType" : BooleanOperationType.SUBTRACTION, "tools" : qUnion([Q0]), "targets" : qUnion([Q1, Q2, Q3]), "keepTools" : true});
        }
        {
            var Q0;
            Q0=makeQuery(id+"F17.opExtrude","SWEPT_BODY",BODY,{"disambiguationData":[OSD([sQuery(id+"F16.wireOp",EDGE,"E49.0.0"),sQuery(id+"F16.wireOp",EDGE,"E49.0.1"),sQuery(id+"F16.wireOp",EDGE,"E49.0.2"),sQuery(id+"F16.wireOp",EDGE,"E49.0.3"),sQuery(id+"F16.wireOp",EDGE,"E49.0.4"),sQuery(id+"F16.wireOp",EDGE,"E49.0.5"),sQuery(id+"F16.wireOp",EDGE,"E49.0.6"),sQuery(id+"F16.wireOp",EDGE,"E49.0.7"),sQuery(id+"F16.wireOp",EDGE,"E49.0.8"),sQuery(id+"F16.wireOp",EDGE,"E49.0.9"),sQuery(id+"F16.wireOp",EDGE,"E49.0.10"),sQuery(id+"F16.wireOp",EDGE,"E49.0.11"),sQuery(id+"F16.wireOp",EDGE,"E49.0.12"),sQuery(id+"F16.wireOp",EDGE,"E49.0.13"),sQuery(id+"F16.wireOp",EDGE,"E49.0.14"),sQuery(id+"F16.wireOp",EDGE,"E49.0.15"),sQuery(id+"F16.wireOp",EDGE,"E49.0.16"),sQuery(id+"F16.wireOp",EDGE,"E49.0.17"),sQuery(id+"F16.wireOp",EDGE,"E49.0.18"),sQuery(id+"F16.wireOp",EDGE,"E49.0.19"),sQuery(id+"F16.wireOp",EDGE,"E49.0.20"),sQuery(id+"F16.wireOp",EDGE,"E49.0.21"),sQuery(id+"F16.wireOp",EDGE,"E49.0.22"),sQuery(id+"F16.wireOp",EDGE,"E49.0.23")])]});
            var Q1;
            Q1=makeQuery(id+"F19.opExtrude","SWEPT_BODY",BODY,{"disambiguationData":[OSD([sQuery(id+"F18.wireOp",EDGE,"E50.bottom"),sQuery(id+"F18.wireOp",EDGE,"E50.top"),sQuery(id+"F18.wireOp",EDGE,"E50.left"),sQuery(id+"F18.wireOp",EDGE,"E50.right"),sQuery(id+"F18.wireOp",EDGE,"E51.bottom"),sQuery(id+"F18.wireOp",EDGE,"E51.top"),sQuery(id+"F18.wireOp",EDGE,"E51.right"),sQuery(id+"F18.wireOp",EDGE,"E52.bottom"),sQuery(id+"F18.wireOp",EDGE,"E52.top"),sQuery(id+"F18.wireOp",EDGE,"E52.right"),sQuery(id+"F18.wireOp",EDGE,"E56.trimOffspring"),sQuery(id+"F18.wireOp",EDGE,"E57.trimOffspring"),sQuery(id+"F18.wireOp",EDGE,"E58.top"),sQuery(id+"F18.wireOp",EDGE,"E58.right"),sQuery(id+"F18.wireOp",EDGE,"E59.top"),sQuery(id+"F18.wireOp",EDGE,"E59.left"),sQuery(id+"F18.wireOp",EDGE,"E59.right"),sQuery(id+"F18.wireOp",EDGE,"E60.top"),sQuery(id+"F18.wireOp",EDGE,"E60.left"),sQuery(id+"F18.wireOp",EDGE,"E60.right"),sQuery(id+"F18.wireOp",EDGE,"E61.top"),sQuery(id+"F18.wireOp",EDGE,"E61.left"),sQuery(id+"F18.wireOp",EDGE,"E61.right"),sQuery(id+"F18.wireOp",EDGE,"E62.top"),sQuery(id+"F18.wireOp",EDGE,"E62.left"),sQuery(id+"F18.wireOp",EDGE,"E62.right"),sQuery(id+"F18.wireOp",EDGE,"E63.top"),sQuery(id+"F18.wireOp",EDGE,"E63.right"),sQuery(id+"F18.wireOp",EDGE,"E64.top"),sQuery(id+"F18.wireOp",EDGE,"E64.left"),sQuery(id+"F18.wireOp",EDGE,"E64.right"),sQuery(id+"F18.wireOp",EDGE,"E65.top"),sQuery(id+"F18.wireOp",EDGE,"E65.left"),sQuery(id+"F18.wireOp",EDGE,"E65.right"),sQuery(id+"F18.wireOp",EDGE,"E66.top"),sQuery(id+"F18.wireOp",EDGE,"E66.left"),sQuery(id+"F18.wireOp",EDGE,"E66.right"),sQuery(id+"F18.wireOp",EDGE,"E67.top"),sQuery(id+"F18.wireOp",EDGE,"E67.left"),sQuery(id+"F18.wireOp",EDGE,"E67.right"),sQuery(id+"F18.wireOp",EDGE,"E73.trimOffspring"),sQuery(id+"F18.wireOp",EDGE,"E74.trimOffspring"),sQuery(id+"F18.wireOp",EDGE,"E75.trimOffspring"),sQuery(id+"F18.wireOp",EDGE,"E76.trimOffspring"),sQuery(id+"F18.wireOp",EDGE,"E77.trimOffspring"),sQuery(id+"F18.wireOp",EDGE,"E78.trimOffspring"),sQuery(id+"F18.wireOp",EDGE,"E79.trimOffspring"),sQuery(id+"F18.wireOp",EDGE,"E80.trimOffspring")])]});
            var Q2;
            Q2=makeQuery(id+"F15.opExtrude","SWEPT_BODY",BODY,{"disambiguationData":[OSD([sQuery(id+"F14.wireOp",EDGE,"E30.right"),sQuery(id+"F14.wireOp",EDGE,"E31.bottom"),sQuery(id+"F14.wireOp",EDGE,"E31.top"),sQuery(id+"F14.wireOp",EDGE,"E32.bottom"),sQuery(id+"F14.wireOp",EDGE,"E32.top"),sQuery(id+"F14.wireOp",EDGE,"E33.bottom"),sQuery(id+"F14.wireOp",EDGE,"E33.top"),sQuery(id+"F14.wireOp",EDGE,"E33.left"),sQuery(id+"F14.wireOp",EDGE,"E34"),sQuery(id+"F14.wireOp",EDGE,"E35"),sQuery(id+"F14.wireOp",EDGE,"E36"),sQuery(id+"F14.wireOp",EDGE,"E37"),sQuery(id+"F14.wireOp",EDGE,"E38.trimOffspring"),sQuery(id+"F14.wireOp",EDGE,"E39.trimOffspring"),sQuery(id+"F14.wireOp",EDGE,"E40.left"),sQuery(id+"F14.wireOp",EDGE,"E40.right"),sQuery(id+"F14.wireOp",EDGE,"E41.left"),sQuery(id+"F14.wireOp",EDGE,"E41.right"),sQuery(id+"F14.wireOp",EDGE,"E40.top"),sQuery(id+"F14.wireOp",EDGE,"E41.top"),sQuery(id+"F14.wireOp",EDGE,"E45"),sQuery(id+"F14.wireOp",EDGE,"E46"),sQuery(id+"F14.wireOp",EDGE,"E47"),sQuery(id+"F14.wireOp",EDGE,"E48")])]});
            var Q3;
            Q3=makeQuery(id+"F13.opExtrude","SWEPT_BODY",BODY,{"disambiguationData":[OSD([sQuery(id+"F12.wireOp",EDGE,"E16.0.2"),sQuery(id+"F12.wireOp",EDGE,"E18"),sQuery(id+"F12.wireOp",EDGE,"E19"),sQuery(id+"F12.wireOp",EDGE,"E20"),sQuery(id+"F12.wireOp",EDGE,"E21"),sQuery(id+"F12.wireOp",EDGE,"E22"),sQuery(id+"F12.wireOp",EDGE,"E23.bottom"),sQuery(id+"F12.wireOp",EDGE,"E23.top"),sQuery(id+"F12.wireOp",EDGE,"E23.right"),sQuery(id+"F12.wireOp",EDGE,"E24.bottom"),sQuery(id+"F12.wireOp",EDGE,"E24.top"),sQuery(id+"F12.wireOp",EDGE,"E24.right"),sQuery(id+"F12.wireOp",EDGE,"E25.bottom"),sQuery(id+"F12.wireOp",EDGE,"E25.top"),sQuery(id+"F12.wireOp",EDGE,"E25.right")])]});
            booleanBodies(context, id + "F21", {"operationType" : BooleanOperationType.SUBTRACTION, "tools" : qUnion([Q0, Q1, Q2]), "targets" : qUnion([Q3]), "keepTools" : true});
        }
        {
            var Q0;
            Q0=makeQuery(id+"F17.opExtrude","SWEPT_BODY",BODY,{"disambiguationData":[OSD([sQuery(id+"F16.wireOp",EDGE,"E49.0.0"),sQuery(id+"F16.wireOp",EDGE,"E49.0.1"),sQuery(id+"F16.wireOp",EDGE,"E49.0.2"),sQuery(id+"F16.wireOp",EDGE,"E49.0.3"),sQuery(id+"F16.wireOp",EDGE,"E49.0.4"),sQuery(id+"F16.wireOp",EDGE,"E49.0.5"),sQuery(id+"F16.wireOp",EDGE,"E49.0.6"),sQuery(id+"F16.wireOp",EDGE,"E49.0.7"),sQuery(id+"F16.wireOp",EDGE,"E49.0.8"),sQuery(id+"F16.wireOp",EDGE,"E49.0.9"),sQuery(id+"F16.wireOp",EDGE,"E49.0.10"),sQuery(id+"F16.wireOp",EDGE,"E49.0.11"),sQuery(id+"F16.wireOp",EDGE,"E49.0.12"),sQuery(id+"F16.wireOp",EDGE,"E49.0.13"),sQuery(id+"F16.wireOp",EDGE,"E49.0.14"),sQuery(id+"F16.wireOp",EDGE,"E49.0.15"),sQuery(id+"F16.wireOp",EDGE,"E49.0.16"),sQuery(id+"F16.wireOp",EDGE,"E49.0.17"),sQuery(id+"F16.wireOp",EDGE,"E49.0.18"),sQuery(id+"F16.wireOp",EDGE,"E49.0.19"),sQuery(id+"F16.wireOp",EDGE,"E49.0.20"),sQuery(id+"F16.wireOp",EDGE,"E49.0.21"),sQuery(id+"F16.wireOp",EDGE,"E49.0.22"),sQuery(id+"F16.wireOp",EDGE,"E49.0.23")])]});
            var Q1;
            Q1=makeQuery(id+"F13.opExtrude","SWEPT_BODY",BODY,{"disambiguationData":[OSD([sQuery(id+"F12.wireOp",EDGE,"E16.0.2"),sQuery(id+"F12.wireOp",EDGE,"E18"),sQuery(id+"F12.wireOp",EDGE,"E19"),sQuery(id+"F12.wireOp",EDGE,"E20"),sQuery(id+"F12.wireOp",EDGE,"E21"),sQuery(id+"F12.wireOp",EDGE,"E22"),sQuery(id+"F12.wireOp",EDGE,"E23.bottom"),sQuery(id+"F12.wireOp",EDGE,"E23.top"),sQuery(id+"F12.wireOp",EDGE,"E23.right"),sQuery(id+"F12.wireOp",EDGE,"E24.bottom"),sQuery(id+"F12.wireOp",EDGE,"E24.top"),sQuery(id+"F12.wireOp",EDGE,"E24.right"),sQuery(id+"F12.wireOp",EDGE,"E25.bottom"),sQuery(id+"F12.wireOp",EDGE,"E25.top"),sQuery(id+"F12.wireOp",EDGE,"E25.right")])]});
            var Q2;
            Q2=makeQuery(id+"F15.opExtrude","SWEPT_BODY",BODY,{"disambiguationData":[OSD([sQuery(id+"F14.wireOp",EDGE,"E30.right"),sQuery(id+"F14.wireOp",EDGE,"E31.bottom"),sQuery(id+"F14.wireOp",EDGE,"E31.top"),sQuery(id+"F14.wireOp",EDGE,"E32.bottom"),sQuery(id+"F14.wireOp",EDGE,"E32.top"),sQuery(id+"F14.wireOp",EDGE,"E33.bottom"),sQuery(id+"F14.wireOp",EDGE,"E33.top"),sQuery(id+"F14.wireOp",EDGE,"E33.left"),sQuery(id+"F14.wireOp",EDGE,"E34"),sQuery(id+"F14.wireOp",EDGE,"E35"),sQuery(id+"F14.wireOp",EDGE,"E36"),sQuery(id+"F14.wireOp",EDGE,"E37"),sQuery(id+"F14.wireOp",EDGE,"E38.trimOffspring"),sQuery(id+"F14.wireOp",EDGE,"E39.trimOffspring"),sQuery(id+"F14.wireOp",EDGE,"E40.left"),sQuery(id+"F14.wireOp",EDGE,"E40.right"),sQuery(id+"F14.wireOp",EDGE,"E41.left"),sQuery(id+"F14.wireOp",EDGE,"E41.right"),sQuery(id+"F14.wireOp",EDGE,"E40.top"),sQuery(id+"F14.wireOp",EDGE,"E41.top"),sQuery(id+"F14.wireOp",EDGE,"E45"),sQuery(id+"F14.wireOp",EDGE,"E46"),sQuery(id+"F14.wireOp",EDGE,"E47"),sQuery(id+"F14.wireOp",EDGE,"E48")])]});
            var Q3;
            Q3=makeQuery(id+"F11.opExtrude","SWEPT_BODY",BODY,{"disambiguationData":[OSD([sQuery(id+"F10.wireOp",EDGE,"E15.bottom"),sQuery(id+"F10.wireOp",EDGE,"E15.top"),sQuery(id+"F10.wireOp",EDGE,"E15.left"),sQuery(id+"F10.wireOp",EDGE,"E15.right")])]});
            booleanBodies(context, id + "F22", {"operationType" : BooleanOperationType.SUBTRACTION, "tools" : qUnion([Q0, Q1, Q2]), "targets" : qUnion([Q3]), "keepTools" : true});
        }
        {
            var Q0;
            Q0=makeQuery(id+"F15.opExtrude","SWEPT_FACE",FACE,{"disambiguationData":[OSD([sQuery(id+"F14.wireOp",EDGE,"E48")])]});
            var sketch = newSketch(context, id + "F23", { "sketchPlane" : qUnion([Q0])});
            skLineSegment(sketch, "E81.0", {"start": v(60.5, -8.9) * mm, "end": v(-47.34, -12.5) * mm});
            skLineSegment(sketch, "E82.0", {"start": v(-47.34, -12.5) * mm, "end": v(-63.21, -12.5) * mm});
            skLineSegment(sketch, "E83.0", {"start": v(-63.22, -5.71) * mm, "end": v(-63.22, -12.5) * mm});
            skLineSegment(sketch, "E84.0", {"start": v(-63.22, -5.72) * mm, "end": v(-34.93, -5.72) * mm});
            skLineSegment(sketch, "E85", {"start": v(60.5, -5.72) * mm, "end": v(60.5, -8.9) * mm});
            skPoint(sketch, "E86.orphan", {"position": v(-57.5, -5.72) * mm});
            skPoint(sketch, "E87.orphan", {"position": v(-63.22, 70.05) * mm});
            skPoint(sketch, "E88.orphan", {"position": v(-63.22, -15.67) * mm});
            skLineSegment(sketch, "E89.top", {"start": v(34.93, 0) * mm, "end": v(22.23, 0) * mm});
            skLineSegment(sketch, "E89.left", {"start": v(34.93, -5.71) * mm, "end": v(34.93, 0) * mm});
            skLineSegment(sketch, "E89.right", {"start": v(22.23, -5.71) * mm, "end": v(22.23, 0) * mm});
            skLineSegment(sketch, "E90.top", {"start": v(-22.23, 0) * mm, "end": v(-34.93, 0) * mm});
            skLineSegment(sketch, "E90.left", {"start": v(-22.23, -5.71) * mm, "end": v(-22.23, 0) * mm});
            skLineSegment(sketch, "E90.right", {"start": v(-34.93, -5.71) * mm, "end": v(-34.93, 0) * mm});
            skLineSegment(sketch, "E91.trimOffspring", {"start": v(-22.22, -5.72) * mm, "end": v(22.23, -5.72) * mm});
            skLineSegment(sketch, "E92.trimOffspring", {"start": v(34.93, -5.72) * mm, "end": v(60.5, -5.72) * mm});
            skSolve(sketch);
        }
        {
            var Q0;
            Q0 = qSketchRegion(id + "F23", true);
            extrude(context, id + "F24", {"entities" : qUnion([Q0]), "oppositeDirection" : true, "depth" : getVariable(context, 'duron_thick')});
        }
        {
            var Q0;
            Q0=qCreatedBy(makeId("Front.planeOp"),FACE);
            var sketch = newSketch(context, id + "F25", { "sketchPlane" : qUnion([Q0])});
            skLineSegment(sketch, "E93.0", {"start": v(47.34, 66.88) * mm, "end": v(63.21, 66.88) * mm});
            skLineSegment(sketch, "E94.0", {"start": v(47.34, 66.88) * mm, "end": v(-60.5, 57.17) * mm});
            skPoint(sketch, "E95.0", {"position": v(-60.5, 54) * mm});
            skLineSegment(sketch, "E96.0", {"start": v(-60.5, 57.17) * mm, "end": v(-60.5, 54) * mm});
            skLineSegment(sketch, "E97.0", {"start": v(-60.5, 54) * mm, "end": v(-34.93, 54) * mm});
            skLineSegment(sketch, "E98", {"start": v(63.21, 66.88) * mm, "end": v(63.21, 54) * mm});
            skLineSegment(sketch, "E99", {"start": v(63.21, 54) * mm, "end": v(57.5, 54) * mm});
            skLineSegment(sketch, "E100.top", {"start": v(-34.93, 51) * mm, "end": v(-22.23, 51) * mm});
            skLineSegment(sketch, "E100.left", {"start": v(-34.93, 54) * mm, "end": v(-34.93, 51) * mm});
            skLineSegment(sketch, "E100.right", {"start": v(-22.23, 54) * mm, "end": v(-22.23, 51) * mm});
            skLineSegment(sketch, "E101.top", {"start": v(22.23, 51) * mm, "end": v(34.93, 51) * mm});
            skLineSegment(sketch, "E101.left", {"start": v(22.22, 54) * mm, "end": v(22.22, 51) * mm});
            skLineSegment(sketch, "E101.right", {"start": v(34.93, 54) * mm, "end": v(34.93, 51) * mm});
            skLineSegment(sketch, "E102.trimOffspring", {"start": v(-22.22, 54) * mm, "end": v(22.22, 54) * mm});
            skLineSegment(sketch, "E103.trimOffspring", {"start": v(34.93, 54) * mm, "end": v(57.5, 54) * mm});
            skSolve(sketch);
        }
        {
            var Q0;
            Q0 = qSketchRegion(id + "F25", true);
            extrude(context, id + "F26", {"entities" : qUnion([Q0]), "oppositeDirection" : true, "depth" : getVariable(context, 'duron_thick')});
        }
        {
            var Q0;
            Q0=makeQuery(id+"F26.opExtrude","SWEPT_BODY",BODY,{"disambiguationData":[OSD([sQuery(id+"F25.wireOp",EDGE,"E93.0"),sQuery(id+"F25.wireOp",EDGE,"E94.0"),sQuery(id+"F25.wireOp",EDGE,"E96.0"),sQuery(id+"F25.wireOp",EDGE,"E97.0"),sQuery(id+"F25.wireOp",EDGE,"E98"),sQuery(id+"F25.wireOp",EDGE,"E99"),sQuery(id+"F25.wireOp",EDGE,"E100.top"),sQuery(id+"F25.wireOp",EDGE,"E100.left"),sQuery(id+"F25.wireOp",EDGE,"E100.right"),sQuery(id+"F25.wireOp",EDGE,"E101.top"),sQuery(id+"F25.wireOp",EDGE,"E101.left"),sQuery(id+"F25.wireOp",EDGE,"E101.right"),sQuery(id+"F25.wireOp",EDGE,"E102.trimOffspring"),sQuery(id+"F25.wireOp",EDGE,"E103.trimOffspring")])]});
            var Q1;
            Q1=makeQuery(id+"F11.opExtrude","SWEPT_BODY",BODY,{"disambiguationData":[OSD([sQuery(id+"F10.wireOp",EDGE,"E15.bottom"),sQuery(id+"F10.wireOp",EDGE,"E15.top"),sQuery(id+"F10.wireOp",EDGE,"E15.left"),sQuery(id+"F10.wireOp",EDGE,"E15.right")])]});
            var Q2;
            Q2=makeQuery(id+"F17.opExtrude","SWEPT_BODY",BODY,{"disambiguationData":[OSD([sQuery(id+"F16.wireOp",EDGE,"E49.0.0"),sQuery(id+"F16.wireOp",EDGE,"E49.0.1"),sQuery(id+"F16.wireOp",EDGE,"E49.0.2"),sQuery(id+"F16.wireOp",EDGE,"E49.0.3"),sQuery(id+"F16.wireOp",EDGE,"E49.0.4"),sQuery(id+"F16.wireOp",EDGE,"E49.0.5"),sQuery(id+"F16.wireOp",EDGE,"E49.0.6"),sQuery(id+"F16.wireOp",EDGE,"E49.0.7"),sQuery(id+"F16.wireOp",EDGE,"E49.0.8"),sQuery(id+"F16.wireOp",EDGE,"E49.0.9"),sQuery(id+"F16.wireOp",EDGE,"E49.0.10"),sQuery(id+"F16.wireOp",EDGE,"E49.0.11"),sQuery(id+"F16.wireOp",EDGE,"E49.0.12"),sQuery(id+"F16.wireOp",EDGE,"E49.0.13"),sQuery(id+"F16.wireOp",EDGE,"E49.0.14"),sQuery(id+"F16.wireOp",EDGE,"E49.0.15"),sQuery(id+"F16.wireOp",EDGE,"E49.0.16"),sQuery(id+"F16.wireOp",EDGE,"E49.0.17"),sQuery(id+"F16.wireOp",EDGE,"E49.0.18"),sQuery(id+"F16.wireOp",EDGE,"E49.0.19"),sQuery(id+"F16.wireOp",EDGE,"E49.0.20"),sQuery(id+"F16.wireOp",EDGE,"E49.0.21"),sQuery(id+"F16.wireOp",EDGE,"E49.0.22"),sQuery(id+"F16.wireOp",EDGE,"E49.0.23")])]});
            booleanBodies(context, id + "F27", {"operationType" : BooleanOperationType.SUBTRACTION, "tools" : qUnion([Q0]), "targets" : qUnion([Q1, Q2]), "keepTools" : true});
        }
        {
            var Q0;
            Q0=makeQuery(id+"F24.opExtrude","SWEPT_BODY",BODY,{"disambiguationData":[OSD([sQuery(id+"F23.wireOp",EDGE,"E81.0"),sQuery(id+"F23.wireOp",EDGE,"E82.0"),sQuery(id+"F23.wireOp",EDGE,"E83.0"),sQuery(id+"F23.wireOp",EDGE,"E84.0"),sQuery(id+"F23.wireOp",EDGE,"E85"),sQuery(id+"F23.wireOp",EDGE,"E89.top"),sQuery(id+"F23.wireOp",EDGE,"E89.left"),sQuery(id+"F23.wireOp",EDGE,"E89.right"),sQuery(id+"F23.wireOp",EDGE,"E90.top"),sQuery(id+"F23.wireOp",EDGE,"E90.left"),sQuery(id+"F23.wireOp",EDGE,"E90.right"),sQuery(id+"F23.wireOp",EDGE,"E91.trimOffspring"),sQuery(id+"F23.wireOp",EDGE,"E92.trimOffspring")])]});
            var Q1;
            Q1=makeQuery(id+"F15.opExtrude","SWEPT_BODY",BODY,{"disambiguationData":[OSD([sQuery(id+"F14.wireOp",EDGE,"E30.right"),sQuery(id+"F14.wireOp",EDGE,"E31.bottom"),sQuery(id+"F14.wireOp",EDGE,"E31.top"),sQuery(id+"F14.wireOp",EDGE,"E32.bottom"),sQuery(id+"F14.wireOp",EDGE,"E32.top"),sQuery(id+"F14.wireOp",EDGE,"E33.bottom"),sQuery(id+"F14.wireOp",EDGE,"E33.top"),sQuery(id+"F14.wireOp",EDGE,"E33.left"),sQuery(id+"F14.wireOp",EDGE,"E34"),sQuery(id+"F14.wireOp",EDGE,"E35"),sQuery(id+"F14.wireOp",EDGE,"E36"),sQuery(id+"F14.wireOp",EDGE,"E37"),sQuery(id+"F14.wireOp",EDGE,"E38.trimOffspring"),sQuery(id+"F14.wireOp",EDGE,"E39.trimOffspring"),sQuery(id+"F14.wireOp",EDGE,"E40.left"),sQuery(id+"F14.wireOp",EDGE,"E40.right"),sQuery(id+"F14.wireOp",EDGE,"E41.left"),sQuery(id+"F14.wireOp",EDGE,"E41.right"),sQuery(id+"F14.wireOp",EDGE,"E40.top"),sQuery(id+"F14.wireOp",EDGE,"E41.top"),sQuery(id+"F14.wireOp",EDGE,"E45"),sQuery(id+"F14.wireOp",EDGE,"E46"),sQuery(id+"F14.wireOp",EDGE,"E47"),sQuery(id+"F14.wireOp",EDGE,"E48")])]});
            var Q2;
            Q2=makeQuery(id+"F11.opExtrude","SWEPT_BODY",BODY,{"disambiguationData":[OSD([sQuery(id+"F10.wireOp",EDGE,"E15.bottom"),sQuery(id+"F10.wireOp",EDGE,"E15.top"),sQuery(id+"F10.wireOp",EDGE,"E15.left"),sQuery(id+"F10.wireOp",EDGE,"E15.right")])]});
            booleanBodies(context, id + "F28", {"operationType" : BooleanOperationType.SUBTRACTION, "tools" : qUnion([Q0]), "targets" : qUnion([Q1, Q2]), "keepTools" : true});
        }
        {
            var Q0;
            Q0=makeQuery(id+"F15.opExtrude","CAP_FACE",FACE,{"disambiguationData":[OSD([sQuery(id+"F14.wireOp",EDGE,"E30.right"),sQuery(id+"F14.wireOp",EDGE,"E31.bottom"),sQuery(id+"F14.wireOp",EDGE,"E31.top"),sQuery(id+"F14.wireOp",EDGE,"E32.bottom"),sQuery(id+"F14.wireOp",EDGE,"E32.top"),sQuery(id+"F14.wireOp",EDGE,"E33.bottom"),sQuery(id+"F14.wireOp",EDGE,"E33.top"),sQuery(id+"F14.wireOp",EDGE,"E33.left"),sQuery(id+"F14.wireOp",EDGE,"E34"),sQuery(id+"F14.wireOp",EDGE,"E35"),sQuery(id+"F14.wireOp",EDGE,"E36"),sQuery(id+"F14.wireOp",EDGE,"E37"),sQuery(id+"F14.wireOp",EDGE,"E38.trimOffspring"),sQuery(id+"F14.wireOp",EDGE,"E39.trimOffspring"),sQuery(id+"F14.wireOp",EDGE,"E40.left"),sQuery(id+"F14.wireOp",EDGE,"E40.right"),sQuery(id+"F14.wireOp",EDGE,"E41.left"),sQuery(id+"F14.wireOp",EDGE,"E41.right"),sQuery(id+"F14.wireOp",EDGE,"E40.top"),sQuery(id+"F14.wireOp",EDGE,"E41.top"),sQuery(id+"F14.wireOp",EDGE,"E45"),sQuery(id+"F14.wireOp",EDGE,"E46"),sQuery(id+"F14.wireOp",EDGE,"E47"),sQuery(id+"F14.wireOp",EDGE,"E48")])],"isStart":false});
            var sketch = newSketch(context, id + "F29", { "sketchPlane" : qUnion([Q0])});
            skLineSegment(sketch, "E104.bottom", {"start": v(-51.78, -75.4) * mm, "end": v(-34.1, -75.4) * mm});
            skLineSegment(sketch, "E104.top", {"start": v(-51.79, 77.4) * mm, "end": v(-34.1, 77.4) * mm});
            skLineSegment(sketch, "E104.left", {"start": v(-51.78, -75.4) * mm, "end": v(-51.79, 77.4) * mm});
            skLineSegment(sketch, "E104.right", {"start": v(-34.1, -75.4) * mm, "end": v(-34.1, 77.4) * mm});
            skLineSegment(sketch, "E105.bottom", {"start": v(34.1, -75.4) * mm, "end": v(48.93, -75.4) * mm});
            skLineSegment(sketch, "E105.top", {"start": v(34.1, 77.4) * mm, "end": v(48.93, 77.4) * mm});
            skLineSegment(sketch, "E105.left", {"start": v(34.1, -75.4) * mm, "end": v(34.1, 77.4) * mm});
            skLineSegment(sketch, "E105.right", {"start": v(48.93, -75.4) * mm, "end": v(48.93, 77.4) * mm});
            skCircle(sketch, "E106", {"center": v(-25.5, -75.5) * mm, "radius": 2 * mm});
            skCircle(sketch, "E107", {"center": v(25.5, -75.5) * mm, "radius": 2 * mm});
            skCircle(sketch, "E108", {"center": v(-25.5, 74.5) * mm, "radius": 2 * mm});
            skCircle(sketch, "E109", {"center": v(25.5, 74.5) * mm, "radius": 2 * mm});
            skLineSegment(sketch, "E110.bottom", {"start": v(-51.79, -35.56) * mm, "end": v(48.93, -35.56) * mm});
            skLineSegment(sketch, "E110.top", {"start": v(-51.79, -44.13) * mm, "end": v(48.93, -44.13) * mm});
            skLineSegment(sketch, "E110.left", {"start": v(-51.78, -44.13) * mm, "end": v(-51.78, -35.56) * mm});
            skLineSegment(sketch, "E110.right", {"start": v(48.93, -44.13) * mm, "end": v(48.93, -35.56) * mm});
            skLineSegment(sketch, "E111.bottom", {"start": v(-51.78, -4.29) * mm, "end": v(48.93, -4.29) * mm});
            skLineSegment(sketch, "E111.top", {"start": v(-51.78, 4.29) * mm, "end": v(48.93, 4.29) * mm});
            skLineSegment(sketch, "E111.left", {"start": v(-51.78, -4.29) * mm, "end": v(-51.78, 4.29) * mm});
            skLineSegment(sketch, "E111.right", {"start": v(48.93, -4.29) * mm, "end": v(48.93, 4.29) * mm});
            skLineSegment(sketch, "E112.bottom", {"start": v(-51.79, 44.13) * mm, "end": v(48.93, 44.13) * mm});
            skLineSegment(sketch, "E112.top", {"start": v(-51.79, 35.56) * mm, "end": v(48.93, 35.56) * mm});
            skLineSegment(sketch, "E112.left", {"start": v(-51.78, 35.56) * mm, "end": v(-51.78, 44.13) * mm});
            skLineSegment(sketch, "E112.right", {"start": v(48.93, 35.56) * mm, "end": v(48.93, 44.13) * mm});
            skLineSegment(sketch, "E113", {"start": v(-42.94, -75.4) * mm, "end": v(-42.94, -44.13) * mm, "construction": true});
            skLineSegment(sketch, "E114", {"start": v(-42.94, -35.56) * mm, "end": v(-42.94, -4.29) * mm, "construction": true});
            skSolve(sketch);
        }
        {
            var Q0;
            Q0=makeQuery(id+"F29.imprint","IMPRINT",FACE,{"disambiguationData":[TD([[makeQuery(id+"F29.imprint","IMPRINT",EDGE,{"derivedFrom":sQuery(id+"F29.wireOp",EDGE,"E106")}),1.0]])]});
            var Q1;
            Q1=makeQuery(id+"F29.imprint","IMPRINT",FACE,{"disambiguationData":[TD([[makeQuery(id+"F29.imprint","IMPRINT",EDGE,{"derivedFrom":sQuery(id+"F29.wireOp",EDGE,"E107")}),1.0]])]});
            var Q2;
            Q2=makeQuery(id+"F29.imprint","IMPRINT",FACE,{"disambiguationData":[TD([[makeQuery(id+"F29.imprint","IMPRINT",EDGE,{"derivedFrom":sQuery(id+"F29.wireOp",EDGE,"E108")}),1.0]])]});
            var Q3;
            Q3=makeQuery(id+"F29.imprint","IMPRINT",FACE,{"disambiguationData":[TD([[makeQuery(id+"F29.imprint","IMPRINT",EDGE,{"derivedFrom":sQuery(id+"F29.wireOp",EDGE,"E109")}),1.0]])]});
            var Q4;
            {var subQ0=sQuery(id+"F29.wireOp",EDGE,"E104.bottom");Q4=makeQuery(id+"F29.imprint","IMPRINT",FACE,{"disambiguationData":[TD([[makeQuery(id+"F29.imprint","IMPRINT",EDGE,{"derivedFrom":subQ0}),1.0]])]});}
            var Q5;
            {var subQ0=sQuery(id+"F29.wireOp",EDGE,"E104.top");Q5=makeQuery(id+"F29.imprint","IMPRINT",FACE,{"disambiguationData":[TD([[makeQuery(id+"F29.imprint","IMPRINT",EDGE,{"derivedFrom":subQ0}),-1.0]])]});}
            var Q6;
            {var subQ0=sQuery(id+"F29.wireOp",EDGE,"E105.bottom");Q6=makeQuery(id+"F29.imprint","IMPRINT",FACE,{"disambiguationData":[TD([[makeQuery(id+"F29.imprint","IMPRINT",EDGE,{"derivedFrom":subQ0}),1.0]])]});}
            var Q7;
            {var subQ0=sQuery(id+"F29.wireOp",EDGE,"E105.top");Q7=makeQuery(id+"F29.imprint","IMPRINT",FACE,{"disambiguationData":[TD([[makeQuery(id+"F29.imprint","IMPRINT",EDGE,{"derivedFrom":subQ0}),-1.0]])]});}
            var Q8;
            {var subQ0=sQuery(id+"F29.wireOp",EDGE,"E110.bottom");var subQ5=sQuery(id+"F29.wireOp",EDGE,"E104.right");var subQ6=makeQuery(id+"F29.imprint","INTERSECT",VERTEX,{"derivedFrom":[subQ5,subQ0]});Q8=makeQuery(id+"F29.imprint","IMPRINT",FACE,{"disambiguationData":[TD([[makeQuery(id+"F29.imprint","IMPRINT",EDGE,{"disambiguationData":[TD([[subQ6,-1.0]])],"derivedFrom":subQ5}),1.0]])]});}
            var Q9;
            {var subQ0=sQuery(id+"F29.wireOp",EDGE,"E111.top");var subQ5=sQuery(id+"F29.wireOp",EDGE,"E104.right");var subQ6=makeQuery(id+"F29.imprint","INTERSECT",VERTEX,{"derivedFrom":[subQ5,subQ0]});Q9=makeQuery(id+"F29.imprint","IMPRINT",FACE,{"disambiguationData":[TD([[makeQuery(id+"F29.imprint","IMPRINT",EDGE,{"disambiguationData":[TD([[subQ6,-1.0]])],"derivedFrom":subQ5}),1.0]])]});}
            var Q10;
            {var subQ0=sQuery(id+"F29.wireOp",EDGE,"E110.bottom");var subQ1=sQuery(id+"F29.wireOp",EDGE,"E105.left");var subQ2=makeQuery(id+"F29.imprint","INTERSECT",VERTEX,{"derivedFrom":[subQ1,subQ0]});Q10=makeQuery(id+"F29.imprint","IMPRINT",FACE,{"disambiguationData":[TD([[makeQuery(id+"F29.imprint","IMPRINT",EDGE,{"disambiguationData":[TD([[subQ2,-1.0]])],"derivedFrom":subQ1}),-1.0]])]});}
            var Q11;
            {var subQ0=sQuery(id+"F29.wireOp",EDGE,"E111.top");var subQ1=sQuery(id+"F29.wireOp",EDGE,"E105.left");var subQ2=makeQuery(id+"F29.imprint","INTERSECT",VERTEX,{"derivedFrom":[subQ1,subQ0]});Q11=makeQuery(id+"F29.imprint","IMPRINT",FACE,{"disambiguationData":[TD([[makeQuery(id+"F29.imprint","IMPRINT",EDGE,{"disambiguationData":[TD([[subQ2,-1.0]])],"derivedFrom":subQ1}),-1.0]])]});}
            extrude(context, id + "F30", {"entities" : qUnion([Q0, Q1, Q2, Q3, Q4, Q5, Q6, Q7, Q8, Q9, Q10, Q11]), "operationType" : NewBodyOperationType.REMOVE, "endBound" : BoundingType.THROUGH_ALL, "oppositeDirection" : true, "depth" : 25.4 * mm});
        }
        {
            var Q0;
            Q0=makeQuery(id+"F30.boolean.opBoolean","COPY",EDGE,{"derivedFrom":makeQuery(id+"F30.opExtrude","SWEPT_EDGE",EDGE,{"disambiguationData":[OSD([sQuery(id+"F29.wireOp",EDGE,"E105.right"),sQuery(id+"F29.wireOp",EDGE,"E112.bottom"),sQuery(id+"F29.wireOp",EDGE,"E112.right")])]})});
            var Q1;
            Q1=makeQuery(id+"F30.boolean.opBoolean","COPY",EDGE,{"derivedFrom":makeQuery(id+"F30.opExtrude","SWEPT_EDGE",EDGE,{"disambiguationData":[OSD([sQuery(id+"F29.wireOp",EDGE,"E105.right"),sQuery(id+"F29.wireOp",EDGE,"E111.top"),sQuery(id+"F29.wireOp",EDGE,"E111.right")])]})});
            var Q2;
            Q2=makeQuery(id+"F30.boolean.opBoolean","COPY",EDGE,{"derivedFrom":makeQuery(id+"F30.opExtrude","SWEPT_EDGE",EDGE,{"disambiguationData":[OSD([sQuery(id+"F29.wireOp",EDGE,"E105.right"),sQuery(id+"F29.wireOp",EDGE,"E110.bottom"),sQuery(id+"F29.wireOp",EDGE,"E110.right")])]})});
            var Q3;
            Q3=makeQuery(id+"F30.boolean.opBoolean","COPY",EDGE,{"derivedFrom":makeQuery(id+"F30.opExtrude","SWEPT_EDGE",EDGE,{"disambiguationData":[OSD([sQuery(id+"F29.wireOp",EDGE,"E105.bottom"),sQuery(id+"F29.wireOp",EDGE,"E105.right")])]})});
            var Q4;
            Q4=makeQuery(id+"F30.boolean.opBoolean","COPY",EDGE,{"derivedFrom":makeQuery(id+"F30.opExtrude","SWEPT_EDGE",EDGE,{"disambiguationData":[OSD([sQuery(id+"F29.wireOp",EDGE,"E104.bottom"),sQuery(id+"F29.wireOp",EDGE,"E104.right")])]})});
            var Q5;
            Q5=makeQuery(id+"F30.boolean.opBoolean","COPY",EDGE,{"derivedFrom":makeQuery(id+"F30.opExtrude","SWEPT_EDGE",EDGE,{"disambiguationData":[OSD([sQuery(id+"F29.wireOp",EDGE,"E104.right"),sQuery(id+"F29.wireOp",EDGE,"E110.bottom")])]})});
            var Q6;
            Q6=makeQuery(id+"F30.boolean.opBoolean","COPY",EDGE,{"derivedFrom":makeQuery(id+"F30.opExtrude","SWEPT_EDGE",EDGE,{"disambiguationData":[OSD([sQuery(id+"F29.wireOp",EDGE,"E104.right"),sQuery(id+"F29.wireOp",EDGE,"E111.top")])]})});
            var Q7;
            Q7=makeQuery(id+"F30.boolean.opBoolean","COPY",EDGE,{"derivedFrom":makeQuery(id+"F30.opExtrude","SWEPT_EDGE",EDGE,{"disambiguationData":[OSD([sQuery(id+"F29.wireOp",EDGE,"E104.right"),sQuery(id+"F29.wireOp",EDGE,"E112.bottom")])]})});
            var Q8;
            Q8=makeQuery(id+"F30.boolean.opBoolean","COPY",EDGE,{"derivedFrom":makeQuery(id+"F30.opExtrude","SWEPT_EDGE",EDGE,{"disambiguationData":[OSD([sQuery(id+"F29.wireOp",EDGE,"E105.right"),sQuery(id+"F29.wireOp",EDGE,"E110.top"),sQuery(id+"F29.wireOp",EDGE,"E110.right")])]})});
            var Q9;
            Q9=makeQuery(id+"F30.boolean.opBoolean","COPY",EDGE,{"derivedFrom":makeQuery(id+"F30.opExtrude","SWEPT_EDGE",EDGE,{"disambiguationData":[OSD([sQuery(id+"F29.wireOp",EDGE,"E105.right"),sQuery(id+"F29.wireOp",EDGE,"E111.bottom"),sQuery(id+"F29.wireOp",EDGE,"E111.right")])]})});
            var Q10;
            Q10=makeQuery(id+"F30.boolean.opBoolean","COPY",EDGE,{"derivedFrom":makeQuery(id+"F30.opExtrude","SWEPT_EDGE",EDGE,{"disambiguationData":[OSD([sQuery(id+"F29.wireOp",EDGE,"E105.right"),sQuery(id+"F29.wireOp",EDGE,"E112.top"),sQuery(id+"F29.wireOp",EDGE,"E112.right")])]})});
            var Q11;
            Q11=makeQuery(id+"F30.boolean.opBoolean","COPY",EDGE,{"derivedFrom":makeQuery(id+"F30.opExtrude","SWEPT_EDGE",EDGE,{"disambiguationData":[OSD([sQuery(id+"F29.wireOp",EDGE,"E105.top"),sQuery(id+"F29.wireOp",EDGE,"E105.right")])]})});
            var Q12;
            Q12=makeQuery(id+"F30.boolean.opBoolean","COPY",EDGE,{"derivedFrom":makeQuery(id+"F30.opExtrude","SWEPT_EDGE",EDGE,{"disambiguationData":[OSD([sQuery(id+"F29.wireOp",EDGE,"E104.top"),sQuery(id+"F29.wireOp",EDGE,"E104.right")])]})});
            var Q13;
            Q13=makeQuery(id+"F30.boolean.opBoolean","COPY",EDGE,{"derivedFrom":makeQuery(id+"F30.opExtrude","SWEPT_EDGE",EDGE,{"disambiguationData":[OSD([sQuery(id+"F29.wireOp",EDGE,"E104.right"),sQuery(id+"F29.wireOp",EDGE,"E112.top")])]})});
            var Q14;
            Q14=makeQuery(id+"F30.boolean.opBoolean","COPY",EDGE,{"derivedFrom":makeQuery(id+"F30.opExtrude","SWEPT_EDGE",EDGE,{"disambiguationData":[OSD([sQuery(id+"F29.wireOp",EDGE,"E104.right"),sQuery(id+"F29.wireOp",EDGE,"E111.bottom")])]})});
            var Q15;
            Q15=makeQuery(id+"F30.boolean.opBoolean","COPY",EDGE,{"derivedFrom":makeQuery(id+"F30.opExtrude","SWEPT_EDGE",EDGE,{"disambiguationData":[OSD([sQuery(id+"F29.wireOp",EDGE,"E104.right"),sQuery(id+"F29.wireOp",EDGE,"E110.top")])]})});
            var Q16;
            Q16=makeQuery(id+"F30.boolean.opBoolean","COPY",EDGE,{"derivedFrom":makeQuery(id+"F30.opExtrude","SWEPT_EDGE",EDGE,{"disambiguationData":[OSD([sQuery(id+"F29.wireOp",EDGE,"E105.left"),sQuery(id+"F29.wireOp",EDGE,"E110.top")])]})});
            var Q17;
            Q17=makeQuery(id+"F30.boolean.opBoolean","COPY",EDGE,{"derivedFrom":makeQuery(id+"F30.opExtrude","SWEPT_EDGE",EDGE,{"disambiguationData":[OSD([sQuery(id+"F29.wireOp",EDGE,"E105.left"),sQuery(id+"F29.wireOp",EDGE,"E111.bottom")])]})});
            var Q18;
            Q18=makeQuery(id+"F30.boolean.opBoolean","COPY",EDGE,{"derivedFrom":makeQuery(id+"F30.opExtrude","SWEPT_EDGE",EDGE,{"disambiguationData":[OSD([sQuery(id+"F29.wireOp",EDGE,"E105.left"),sQuery(id+"F29.wireOp",EDGE,"E112.top")])]})});
            var Q19;
            Q19=makeQuery(id+"F30.boolean.opBoolean","COPY",EDGE,{"derivedFrom":makeQuery(id+"F30.opExtrude","SWEPT_EDGE",EDGE,{"disambiguationData":[OSD([sQuery(id+"F29.wireOp",EDGE,"E105.top"),sQuery(id+"F29.wireOp",EDGE,"E105.left")])]})});
            var Q20;
            Q20=makeQuery(id+"F30.boolean.opBoolean","COPY",EDGE,{"derivedFrom":makeQuery(id+"F30.opExtrude","SWEPT_EDGE",EDGE,{"disambiguationData":[OSD([sQuery(id+"F29.wireOp",EDGE,"E104.top"),sQuery(id+"F29.wireOp",EDGE,"E104.left")])]})});
            var Q21;
            Q21=makeQuery(id+"F30.boolean.opBoolean","COPY",EDGE,{"derivedFrom":makeQuery(id+"F30.opExtrude","SWEPT_EDGE",EDGE,{"disambiguationData":[OSD([sQuery(id+"F29.wireOp",EDGE,"E104.left"),sQuery(id+"F29.wireOp",EDGE,"E112.top"),sQuery(id+"F29.wireOp",EDGE,"E112.left")])]})});
            var Q22;
            Q22=makeQuery(id+"F30.boolean.opBoolean","COPY",EDGE,{"derivedFrom":makeQuery(id+"F30.opExtrude","SWEPT_EDGE",EDGE,{"disambiguationData":[OSD([sQuery(id+"F29.wireOp",EDGE,"E104.left"),sQuery(id+"F29.wireOp",EDGE,"E111.bottom"),sQuery(id+"F29.wireOp",EDGE,"E111.left")])]})});
            var Q23;
            Q23=makeQuery(id+"F30.boolean.opBoolean","COPY",EDGE,{"derivedFrom":makeQuery(id+"F30.opExtrude","SWEPT_EDGE",EDGE,{"disambiguationData":[OSD([sQuery(id+"F29.wireOp",EDGE,"E104.left"),sQuery(id+"F29.wireOp",EDGE,"E110.top"),sQuery(id+"F29.wireOp",EDGE,"E110.left")])]})});
            var Q24;
            Q24=makeQuery(id+"F30.boolean.opBoolean","COPY",EDGE,{"derivedFrom":makeQuery(id+"F30.opExtrude","SWEPT_EDGE",EDGE,{"disambiguationData":[OSD([sQuery(id+"F29.wireOp",EDGE,"E105.left"),sQuery(id+"F29.wireOp",EDGE,"E112.bottom")])]})});
            var Q25;
            Q25=makeQuery(id+"F30.boolean.opBoolean","COPY",EDGE,{"derivedFrom":makeQuery(id+"F30.opExtrude","SWEPT_EDGE",EDGE,{"disambiguationData":[OSD([sQuery(id+"F29.wireOp",EDGE,"E105.left"),sQuery(id+"F29.wireOp",EDGE,"E111.top")])]})});
            var Q26;
            Q26=makeQuery(id+"F30.boolean.opBoolean","COPY",EDGE,{"derivedFrom":makeQuery(id+"F30.opExtrude","SWEPT_EDGE",EDGE,{"disambiguationData":[OSD([sQuery(id+"F29.wireOp",EDGE,"E105.left"),sQuery(id+"F29.wireOp",EDGE,"E110.bottom")])]})});
            var Q27;
            Q27=makeQuery(id+"F30.boolean.opBoolean","COPY",EDGE,{"derivedFrom":makeQuery(id+"F30.opExtrude","SWEPT_EDGE",EDGE,{"disambiguationData":[OSD([sQuery(id+"F29.wireOp",EDGE,"E105.bottom"),sQuery(id+"F29.wireOp",EDGE,"E105.left")])]})});
            var Q28;
            Q28=makeQuery(id+"F30.boolean.opBoolean","COPY",EDGE,{"derivedFrom":makeQuery(id+"F30.opExtrude","SWEPT_EDGE",EDGE,{"disambiguationData":[OSD([sQuery(id+"F29.wireOp",EDGE,"E104.bottom"),sQuery(id+"F29.wireOp",EDGE,"E104.left")])]})});
            var Q29;
            Q29=makeQuery(id+"F30.boolean.opBoolean","COPY",EDGE,{"derivedFrom":makeQuery(id+"F30.opExtrude","SWEPT_EDGE",EDGE,{"disambiguationData":[OSD([sQuery(id+"F29.wireOp",EDGE,"E104.left"),sQuery(id+"F29.wireOp",EDGE,"E110.bottom"),sQuery(id+"F29.wireOp",EDGE,"E110.left")])]})});
            var Q30;
            Q30=makeQuery(id+"F30.boolean.opBoolean","COPY",EDGE,{"derivedFrom":makeQuery(id+"F30.opExtrude","SWEPT_EDGE",EDGE,{"disambiguationData":[OSD([sQuery(id+"F29.wireOp",EDGE,"E104.left"),sQuery(id+"F29.wireOp",EDGE,"E111.top"),sQuery(id+"F29.wireOp",EDGE,"E111.left")])]})});
            var Q31;
            Q31=makeQuery(id+"F30.boolean.opBoolean","COPY",EDGE,{"derivedFrom":makeQuery(id+"F30.opExtrude","SWEPT_EDGE",EDGE,{"disambiguationData":[OSD([sQuery(id+"F29.wireOp",EDGE,"E104.left"),sQuery(id+"F29.wireOp",EDGE,"E112.bottom"),sQuery(id+"F29.wireOp",EDGE,"E112.left")])]})});
            fillet(context, id + "F31", {"entities" : qUnion([Q0, Q1, Q2, Q3, Q4, Q5, Q6, Q7, Q8, Q9, Q10, Q11, Q12, Q13, Q14, Q15, Q16, Q17, Q18, Q19, Q20, Q21, Q22, Q23, Q24, Q25, Q26, Q27, Q28, Q29, Q30, Q31]), "radius" : getVariable(context, 'duron_thick'), "tangentPropagation" : true, "allowEdgeOverflow" : false});
        }
        {
            var Q0;
            Q0=makeQuery(id+"F17.opExtrude","CAP_FACE",FACE,{"disambiguationData":[OSD([sQuery(id+"F16.wireOp",EDGE,"E49.0.0"),sQuery(id+"F16.wireOp",EDGE,"E49.0.1"),sQuery(id+"F16.wireOp",EDGE,"E49.0.2"),sQuery(id+"F16.wireOp",EDGE,"E49.0.3"),sQuery(id+"F16.wireOp",EDGE,"E49.0.4"),sQuery(id+"F16.wireOp",EDGE,"E49.0.5"),sQuery(id+"F16.wireOp",EDGE,"E49.0.6"),sQuery(id+"F16.wireOp",EDGE,"E49.0.7"),sQuery(id+"F16.wireOp",EDGE,"E49.0.8"),sQuery(id+"F16.wireOp",EDGE,"E49.0.9"),sQuery(id+"F16.wireOp",EDGE,"E49.0.10"),sQuery(id+"F16.wireOp",EDGE,"E49.0.11"),sQuery(id+"F16.wireOp",EDGE,"E49.0.12"),sQuery(id+"F16.wireOp",EDGE,"E49.0.13"),sQuery(id+"F16.wireOp",EDGE,"E49.0.14"),sQuery(id+"F16.wireOp",EDGE,"E49.0.15"),sQuery(id+"F16.wireOp",EDGE,"E49.0.16"),sQuery(id+"F16.wireOp",EDGE,"E49.0.17"),sQuery(id+"F16.wireOp",EDGE,"E49.0.18"),sQuery(id+"F16.wireOp",EDGE,"E49.0.19"),sQuery(id+"F16.wireOp",EDGE,"E49.0.20"),sQuery(id+"F16.wireOp",EDGE,"E49.0.21"),sQuery(id+"F16.wireOp",EDGE,"E49.0.22"),sQuery(id+"F16.wireOp",EDGE,"E49.0.23")])],"isStart":false});
            var sketch = newSketch(context, id + "F32", { "sketchPlane" : qUnion([Q0])});
            skCircle(sketch, "E115", {"center": v(21.5, -61) * mm, "radius": 25.3 * mm});
            skCircle(sketch, "E116", {"center": v(21.5, -61) * mm, "radius": 14.29 * mm});
            skLineSegment(sketch, "E117", {"start": v(21.5, -61) * mm, "end": v(21.5, -35.7) * mm, "construction": true});
            skLineSegment(sketch, "E118.bottom", {"start": v(19.25, -35.7) * mm, "end": v(23.75, -35.7) * mm});
            skLineSegment(sketch, "E118.top", {"start": v(19.25, -61) * mm, "end": v(23.75, -61) * mm});
            skLineSegment(sketch, "E118.left", {"start": v(19.25, -35.7) * mm, "end": v(19.25, -61) * mm});
            skLineSegment(sketch, "E118.right", {"start": v(23.75, -35.7) * mm, "end": v(23.75, -61) * mm});
            skLineSegment(sketch, "E119.1.0", {"start": v(-1.86, -51.05) * mm, "end": v(22.2, -58.86) * mm});
            skLineSegment(sketch, "E119.1.1", {"start": v(20.8, -63.14) * mm, "end": v(22.2, -58.86) * mm});
            skLineSegment(sketch, "E119.1.2", {"start": v(-3.25, -55.32) * mm, "end": v(20.8, -63.14) * mm});
            skLineSegment(sketch, "E119.1.3", {"start": v(-3.25, -55.32) * mm, "end": v(-1.86, -51.05) * mm});
            skLineSegment(sketch, "E119.2.0", {"start": v(4.81, -80.14) * mm, "end": v(19.68, -59.68) * mm});
            skLineSegment(sketch, "E119.2.1", {"start": v(23.32, -62.32) * mm, "end": v(19.68, -59.68) * mm});
            skLineSegment(sketch, "E119.2.2", {"start": v(8.45, -82.78) * mm, "end": v(23.32, -62.32) * mm});
            skLineSegment(sketch, "E119.2.3", {"start": v(8.45, -82.78) * mm, "end": v(4.81, -80.14) * mm});
            skLineSegment(sketch, "E120.2.3.0", {"start": v(34.55, -82.78) * mm, "end": v(19.68, -62.32) * mm});
            skLineSegment(sketch, "E120.3.3.0", {"start": v(23.32, -59.68) * mm, "end": v(19.68, -62.32) * mm});
            skLineSegment(sketch, "E120.6.3.0", {"start": v(38.19, -80.14) * mm, "end": v(23.32, -59.68) * mm});
            skLineSegment(sketch, "E120.9.3.0", {"start": v(38.19, -80.14) * mm, "end": v(34.55, -82.78) * mm});
            skLineSegment(sketch, "E120.2.4.0", {"start": v(46.25, -55.32) * mm, "end": v(22.2, -63.14) * mm});
            skLineSegment(sketch, "E120.3.4.0", {"start": v(20.8, -58.86) * mm, "end": v(22.2, -63.14) * mm});
            skLineSegment(sketch, "E120.6.4.0", {"start": v(44.86, -51.05) * mm, "end": v(20.8, -58.86) * mm});
            skLineSegment(sketch, "E120.9.4.0", {"start": v(44.86, -51.05) * mm, "end": v(46.25, -55.32) * mm});
            skLineSegment(sketch, "E121.bottom", {"start": v(-35.4, 79.4) * mm, "end": v(35.4, 79.4) * mm});
            skLineSegment(sketch, "E121.top", {"start": v(-35.4, 47.6) * mm, "end": v(35.4, 47.6) * mm});
            skLineSegment(sketch, "E121.left", {"start": v(-35.4, 79.4) * mm, "end": v(-35.4, 47.6) * mm});
            skLineSegment(sketch, "E121.right", {"start": v(35.4, 79.4) * mm, "end": v(35.4, 47.6) * mm});
            skLineSegment(sketch, "E122.bottom", {"start": v(-36.32, 77.35) * mm, "end": v(-34.48, 81.45) * mm});
            skLineSegment(sketch, "E122.top", {"start": v(34.48, 45.55) * mm, "end": v(36.32, 49.65) * mm});
            skLineSegment(sketch, "E122.left", {"start": v(-36.32, 77.35) * mm, "end": v(34.48, 45.55) * mm});
            skLineSegment(sketch, "E122.right", {"start": v(-34.48, 81.45) * mm, "end": v(36.32, 49.65) * mm});
            skLineSegment(sketch, "E123.bottom", {"start": v(-34.48, 45.55) * mm, "end": v(36.32, 77.35) * mm});
            skLineSegment(sketch, "E123.top", {"start": v(-36.32, 49.65) * mm, "end": v(34.48, 81.45) * mm});
            skLineSegment(sketch, "E123.left", {"start": v(34.48, 81.45) * mm, "end": v(36.32, 77.35) * mm});
            skLineSegment(sketch, "E123.right", {"start": v(-36.32, 49.65) * mm, "end": v(-34.48, 45.55) * mm});
            skLineSegment(sketch, "E124.bottom", {"start": v(35.28, 108) * mm, "end": v(-47.97, 108) * mm});
            skLineSegment(sketch, "E124.top", {"start": v(35.28, 88) * mm, "end": v(-47.97, 88) * mm});
            skLineSegment(sketch, "E124.left", {"start": v(35.28, 108) * mm, "end": v(35.28, 88) * mm});
            skLineSegment(sketch, "E124.right", {"start": v(-47.97, 108) * mm, "end": v(-47.97, 88) * mm});
            skSolve(sketch);
        }
        {
            var Q0;
            {var subQ0=sQuery(id+"F32.wireOp",EDGE,"E122.left");var subQ1=sQuery(id+"F32.wireOp",EDGE,"E121.left");var subQ2=makeQuery(id+"F32.imprint","INTERSECT",VERTEX,{"derivedFrom":[subQ1,subQ0]});Q0=makeQuery(id+"F32.imprint","IMPRINT",FACE,{"disambiguationData":[TD([[makeQuery(id+"F32.imprint","IMPRINT",EDGE,{"disambiguationData":[TD([[subQ2,-1.0]])],"derivedFrom":subQ1}),1.0]])]});}
            var Q1;
            {var subQ0=sQuery(id+"F32.wireOp",EDGE,"E122.right");var subQ1=sQuery(id+"F32.wireOp",EDGE,"E121.bottom");var subQ2=makeQuery(id+"F32.imprint","INTERSECT",VERTEX,{"derivedFrom":[subQ1,subQ0]});Q1=makeQuery(id+"F32.imprint","IMPRINT",FACE,{"disambiguationData":[TD([[makeQuery(id+"F32.imprint","IMPRINT",EDGE,{"disambiguationData":[TD([[subQ2,-1.0]])],"derivedFrom":subQ1}),-1.0]])]});}
            var Q2;
            {var subQ0=sQuery(id+"F32.wireOp",EDGE,"E123.bottom");var subQ1=sQuery(id+"F32.wireOp",EDGE,"E121.right");var subQ2=makeQuery(id+"F32.imprint","INTERSECT",VERTEX,{"derivedFrom":[subQ1,subQ0]});Q2=makeQuery(id+"F32.imprint","IMPRINT",FACE,{"disambiguationData":[TD([[makeQuery(id+"F32.imprint","IMPRINT",EDGE,{"disambiguationData":[TD([[subQ2,-1.0]])],"derivedFrom":subQ1}),-1.0]])]});}
            var Q3;
            {var subQ0=sQuery(id+"F32.wireOp",EDGE,"E123.bottom");var subQ1=sQuery(id+"F32.wireOp",EDGE,"E121.top");var subQ2=makeQuery(id+"F32.imprint","INTERSECT",VERTEX,{"derivedFrom":[subQ1,subQ0]});Q3=makeQuery(id+"F32.imprint","IMPRINT",FACE,{"disambiguationData":[TD([[makeQuery(id+"F32.imprint","IMPRINT",EDGE,{"disambiguationData":[TD([[subQ2,-1.0]])],"derivedFrom":subQ1}),1.0]])]});}
            var Q4;
            {var subQ0=sQuery(id+"F32.wireOp",EDGE,"E120.2.4.0");var subQ1=sQuery(id+"F32.wireOp",EDGE,"E115");var subQ2=makeQuery(id+"F32.imprint","INTERSECT",VERTEX,{"derivedFrom":[subQ1,subQ0]});Q4=makeQuery(id+"F32.imprint","IMPRINT",FACE,{"disambiguationData":[TD([[makeQuery(id+"F32.imprint","IMPRINT",EDGE,{"disambiguationData":[TD([[subQ2,1.0]])],"derivedFrom":subQ1}),1.0]])]});}
            var Q5;
            {var subQ0=sQuery(id+"F32.wireOp",EDGE,"E120.6.4.0");var subQ1=sQuery(id+"F32.wireOp",EDGE,"E115");var subQ2=makeQuery(id+"F32.imprint","INTERSECT",VERTEX,{"derivedFrom":[subQ1,subQ0]});Q5=makeQuery(id+"F32.imprint","IMPRINT",FACE,{"disambiguationData":[TD([[makeQuery(id+"F32.imprint","IMPRINT",EDGE,{"disambiguationData":[TD([[subQ2,-1.0]])],"derivedFrom":subQ1}),1.0]])]});}
            var Q6;
            {var subQ0=sQuery(id+"F32.wireOp",EDGE,"E118.left");var subQ1=sQuery(id+"F32.wireOp",EDGE,"E115");var subQ2=makeQuery(id+"F32.imprint","INTERSECT",VERTEX,{"derivedFrom":[subQ1,subQ0]});Q6=makeQuery(id+"F32.imprint","IMPRINT",FACE,{"disambiguationData":[TD([[makeQuery(id+"F32.imprint","IMPRINT",EDGE,{"disambiguationData":[TD([[subQ2,-1.0]])],"derivedFrom":subQ1}),1.0]])]});}
            var Q7;
            {var subQ0=sQuery(id+"F32.wireOp",EDGE,"E119.1.2");var subQ1=sQuery(id+"F32.wireOp",EDGE,"E115");var subQ2=makeQuery(id+"F32.imprint","INTERSECT",VERTEX,{"derivedFrom":[subQ1,subQ0]});Q7=makeQuery(id+"F32.imprint","IMPRINT",FACE,{"disambiguationData":[TD([[makeQuery(id+"F32.imprint","IMPRINT",EDGE,{"disambiguationData":[TD([[subQ2,-1.0]])],"derivedFrom":subQ1}),1.0]])]});}
            var Q8;
            {var subQ0=sQuery(id+"F32.wireOp",EDGE,"E119.2.2");var subQ1=sQuery(id+"F32.wireOp",EDGE,"E115");var subQ2=makeQuery(id+"F32.imprint","INTERSECT",VERTEX,{"derivedFrom":[subQ1,subQ0]});Q8=makeQuery(id+"F32.imprint","IMPRINT",FACE,{"disambiguationData":[TD([[makeQuery(id+"F32.imprint","IMPRINT",EDGE,{"disambiguationData":[TD([[subQ2,-1.0]])],"derivedFrom":subQ1}),1.0]])]});}
            var Q9;
            Q9=makeQuery(id+"F32.imprint","IMPRINT",FACE,{"disambiguationData":[TD([[makeQuery(id+"F32.imprint","IMPRINT",EDGE,{"derivedFrom":sQuery(id+"F32.wireOp",EDGE,"E124.bottom")}),-1.0]])]});
            extrude(context, id + "F33", {"entities" : qUnion([Q0, Q1, Q2, Q3, Q4, Q5, Q6, Q7, Q8, Q9]), "operationType" : NewBodyOperationType.REMOVE, "endBound" : BoundingType.THROUGH_ALL, "oppositeDirection" : true, "depth" : 25.4 * mm});
        }
        {
            var Q0;
            Q0=makeQuery(id+"F33.boolean.opBoolean","COPY",EDGE,{"derivedFrom":makeQuery(id+"F33.opExtrude","SWEPT_EDGE",EDGE,{"disambiguationData":[OSD([sQuery(id+"F32.wireOp",EDGE,"E124.top"),sQuery(id+"F32.wireOp",EDGE,"E124.left")])]})});
            var Q1;
            Q1=makeQuery(id+"F33.boolean.opBoolean","COPY",EDGE,{"derivedFrom":makeQuery(id+"F33.opExtrude","SWEPT_EDGE",EDGE,{"disambiguationData":[OSD([sQuery(id+"F16.wireOp",EDGE,"E49.0.0"),sQuery(id+"F32.wireOp",EDGE,"E124.bottom"),sQuery(id+"F32.wireOp",EDGE,"E124.left")])]})});
            var Q2;
            Q2=makeQuery(id+"F33.boolean.opBoolean","COPY",EDGE,{"derivedFrom":makeQuery(id+"F33.opExtrude","SWEPT_EDGE",EDGE,{"disambiguationData":[OSD([sQuery(id+"F32.wireOp",EDGE,"E124.top"),sQuery(id+"F32.wireOp",EDGE,"E124.right")])]})});
            var Q3;
            Q3=makeQuery(id+"F33.boolean.opBoolean","COPY",EDGE,{"derivedFrom":makeQuery(id+"F33.opExtrude","SWEPT_EDGE",EDGE,{"disambiguationData":[OSD([sQuery(id+"F16.wireOp",EDGE,"E49.0.0"),sQuery(id+"F32.wireOp",EDGE,"E124.bottom"),sQuery(id+"F32.wireOp",EDGE,"E124.right")])]})});
            var Q4;
            Q4=makeQuery(id+"F33.boolean.opBoolean","COPY",EDGE,{"derivedFrom":makeQuery(id+"F33.opExtrude","SWEPT_EDGE",EDGE,{"disambiguationData":[OSD([sQuery(id+"F32.wireOp",EDGE,"E121.left"),sQuery(id+"F32.wireOp",EDGE,"E123.top")])]})});
            var Q5;
            Q5=makeQuery(id+"F33.boolean.opBoolean","COPY",EDGE,{"derivedFrom":makeQuery(id+"F33.opExtrude","SWEPT_EDGE",EDGE,{"disambiguationData":[OSD([sQuery(id+"F32.wireOp",EDGE,"E122.right"),sQuery(id+"F32.wireOp",EDGE,"E123.bottom")])]})});
            var Q6;
            Q6=makeQuery(id+"F33.boolean.opBoolean","COPY",EDGE,{"derivedFrom":makeQuery(id+"F33.opExtrude","SWEPT_EDGE",EDGE,{"disambiguationData":[OSD([sQuery(id+"F32.wireOp",EDGE,"E121.top"),sQuery(id+"F32.wireOp",EDGE,"E123.bottom")])]})});
            var Q7;
            Q7=makeQuery(id+"F33.boolean.opBoolean","COPY",EDGE,{"derivedFrom":makeQuery(id+"F33.opExtrude","SWEPT_EDGE",EDGE,{"disambiguationData":[OSD([sQuery(id+"F32.wireOp",EDGE,"E122.left"),sQuery(id+"F32.wireOp",EDGE,"E123.bottom")])]})});
            var Q8;
            Q8=makeQuery(id+"F33.boolean.opBoolean","COPY",EDGE,{"derivedFrom":makeQuery(id+"F33.opExtrude","SWEPT_EDGE",EDGE,{"disambiguationData":[OSD([sQuery(id+"F32.wireOp",EDGE,"E122.left"),sQuery(id+"F32.wireOp",EDGE,"E123.top")])]})});
            var Q9;
            Q9=makeQuery(id+"F33.boolean.opBoolean","COPY",EDGE,{"derivedFrom":makeQuery(id+"F33.opExtrude","SWEPT_EDGE",EDGE,{"disambiguationData":[OSD([sQuery(id+"F32.wireOp",EDGE,"E122.right"),sQuery(id+"F32.wireOp",EDGE,"E123.top")])]})});
            var Q10;
            Q10=makeQuery(id+"F33.boolean.opBoolean","COPY",EDGE,{"derivedFrom":makeQuery(id+"F33.opExtrude","SWEPT_EDGE",EDGE,{"disambiguationData":[OSD([sQuery(id+"F32.wireOp",EDGE,"E121.left"),sQuery(id+"F32.wireOp",EDGE,"E122.left")])]})});
            var Q11;
            Q11=makeQuery(id+"F33.boolean.opBoolean","COPY",EDGE,{"derivedFrom":makeQuery(id+"F33.opExtrude","SWEPT_EDGE",EDGE,{"disambiguationData":[OSD([sQuery(id+"F32.wireOp",EDGE,"E121.bottom"),sQuery(id+"F32.wireOp",EDGE,"E122.right")])]})});
            var Q12;
            Q12=makeQuery(id+"F33.boolean.opBoolean","COPY",EDGE,{"derivedFrom":makeQuery(id+"F33.opExtrude","SWEPT_EDGE",EDGE,{"disambiguationData":[OSD([sQuery(id+"F32.wireOp",EDGE,"E121.bottom"),sQuery(id+"F32.wireOp",EDGE,"E123.top")])]})});
            var Q13;
            Q13=makeQuery(id+"F33.boolean.opBoolean","COPY",EDGE,{"derivedFrom":makeQuery(id+"F33.opExtrude","SWEPT_EDGE",EDGE,{"disambiguationData":[OSD([sQuery(id+"F32.wireOp",EDGE,"E121.right"),sQuery(id+"F32.wireOp",EDGE,"E123.bottom")])]})});
            var Q14;
            Q14=makeQuery(id+"F33.boolean.opBoolean","COPY",EDGE,{"derivedFrom":makeQuery(id+"F33.opExtrude","SWEPT_EDGE",EDGE,{"disambiguationData":[OSD([sQuery(id+"F32.wireOp",EDGE,"E121.right"),sQuery(id+"F32.wireOp",EDGE,"E122.right")])]})});
            var Q15;
            Q15=makeQuery(id+"F33.boolean.opBoolean","COPY",EDGE,{"derivedFrom":makeQuery(id+"F33.opExtrude","SWEPT_EDGE",EDGE,{"disambiguationData":[OSD([sQuery(id+"F32.wireOp",EDGE,"E121.top"),sQuery(id+"F32.wireOp",EDGE,"E122.left")])]})});
            var Q16;
            Q16=makeQuery(id+"F33.boolean.opBoolean","COPY",EDGE,{"derivedFrom":makeQuery(id+"F33.opExtrude","SWEPT_EDGE",EDGE,{"disambiguationData":[OSD([sQuery(id+"F32.wireOp",EDGE,"E115"),sQuery(id+"F32.wireOp",EDGE,"E119.2.2")])]})});
            var Q17;
            Q17=makeQuery(id+"F33.boolean.opBoolean","COPY",EDGE,{"derivedFrom":makeQuery(id+"F33.opExtrude","SWEPT_EDGE",EDGE,{"disambiguationData":[OSD([sQuery(id+"F32.wireOp",EDGE,"E115"),sQuery(id+"F32.wireOp",EDGE,"E119.2.0")])]})});
            var Q18;
            Q18=makeQuery(id+"F33.boolean.opBoolean","COPY",EDGE,{"derivedFrom":makeQuery(id+"F33.opExtrude","SWEPT_EDGE",EDGE,{"disambiguationData":[OSD([sQuery(id+"F32.wireOp",EDGE,"E116"),sQuery(id+"F32.wireOp",EDGE,"E119.2.2")])]})});
            var Q19;
            Q19=makeQuery(id+"F33.boolean.opBoolean","COPY",EDGE,{"derivedFrom":makeQuery(id+"F33.opExtrude","SWEPT_EDGE",EDGE,{"disambiguationData":[OSD([sQuery(id+"F32.wireOp",EDGE,"E116"),sQuery(id+"F32.wireOp",EDGE,"E119.2.0")])]})});
            var Q20;
            Q20=makeQuery(id+"F33.boolean.opBoolean","COPY",EDGE,{"derivedFrom":makeQuery(id+"F33.opExtrude","SWEPT_EDGE",EDGE,{"disambiguationData":[OSD([sQuery(id+"F32.wireOp",EDGE,"E116"),sQuery(id+"F32.wireOp",EDGE,"E119.1.2")])]})});
            var Q21;
            Q21=makeQuery(id+"F33.boolean.opBoolean","COPY",EDGE,{"derivedFrom":makeQuery(id+"F33.opExtrude","SWEPT_EDGE",EDGE,{"disambiguationData":[OSD([sQuery(id+"F32.wireOp",EDGE,"E115"),sQuery(id+"F32.wireOp",EDGE,"E119.1.2")])]})});
            var Q22;
            Q22=makeQuery(id+"F33.boolean.opBoolean","COPY",EDGE,{"derivedFrom":makeQuery(id+"F33.opExtrude","SWEPT_EDGE",EDGE,{"disambiguationData":[OSD([sQuery(id+"F32.wireOp",EDGE,"E116"),sQuery(id+"F32.wireOp",EDGE,"E119.1.0")])]})});
            var Q23;
            Q23=makeQuery(id+"F33.boolean.opBoolean","COPY",EDGE,{"derivedFrom":makeQuery(id+"F33.opExtrude","SWEPT_EDGE",EDGE,{"disambiguationData":[OSD([sQuery(id+"F32.wireOp",EDGE,"E115"),sQuery(id+"F32.wireOp",EDGE,"E119.1.0")])]})});
            var Q24;
            Q24=makeQuery(id+"F33.boolean.opBoolean","COPY",EDGE,{"derivedFrom":makeQuery(id+"F33.opExtrude","SWEPT_EDGE",EDGE,{"disambiguationData":[OSD([sQuery(id+"F32.wireOp",EDGE,"E115"),sQuery(id+"F32.wireOp",EDGE,"E118.left")])]})});
            var Q25;
            Q25=makeQuery(id+"F33.boolean.opBoolean","COPY",EDGE,{"derivedFrom":makeQuery(id+"F33.opExtrude","SWEPT_EDGE",EDGE,{"disambiguationData":[OSD([sQuery(id+"F32.wireOp",EDGE,"E116"),sQuery(id+"F32.wireOp",EDGE,"E118.left")])]})});
            var Q26;
            Q26=makeQuery(id+"F33.boolean.opBoolean","COPY",EDGE,{"derivedFrom":makeQuery(id+"F33.opExtrude","SWEPT_EDGE",EDGE,{"disambiguationData":[OSD([sQuery(id+"F32.wireOp",EDGE,"E116"),sQuery(id+"F32.wireOp",EDGE,"E118.right")])]})});
            var Q27;
            Q27=makeQuery(id+"F33.boolean.opBoolean","COPY",EDGE,{"derivedFrom":makeQuery(id+"F33.opExtrude","SWEPT_EDGE",EDGE,{"disambiguationData":[OSD([sQuery(id+"F32.wireOp",EDGE,"E115"),sQuery(id+"F32.wireOp",EDGE,"E118.right")])]})});
            var Q28;
            Q28=makeQuery(id+"F33.boolean.opBoolean","COPY",EDGE,{"derivedFrom":makeQuery(id+"F33.opExtrude","SWEPT_EDGE",EDGE,{"disambiguationData":[OSD([sQuery(id+"F32.wireOp",EDGE,"E116"),sQuery(id+"F32.wireOp",EDGE,"E120.6.4.0")])]})});
            var Q29;
            Q29=makeQuery(id+"F33.boolean.opBoolean","COPY",EDGE,{"derivedFrom":makeQuery(id+"F33.opExtrude","SWEPT_EDGE",EDGE,{"disambiguationData":[OSD([sQuery(id+"F32.wireOp",EDGE,"E115"),sQuery(id+"F32.wireOp",EDGE,"E120.6.4.0")])]})});
            var Q30;
            Q30=makeQuery(id+"F33.boolean.opBoolean","COPY",EDGE,{"derivedFrom":makeQuery(id+"F33.opExtrude","SWEPT_EDGE",EDGE,{"disambiguationData":[OSD([sQuery(id+"F32.wireOp",EDGE,"E115"),sQuery(id+"F32.wireOp",EDGE,"E120.2.4.0")])]})});
            var Q31;
            Q31=makeQuery(id+"F33.boolean.opBoolean","COPY",EDGE,{"derivedFrom":makeQuery(id+"F33.opExtrude","SWEPT_EDGE",EDGE,{"disambiguationData":[OSD([sQuery(id+"F32.wireOp",EDGE,"E116"),sQuery(id+"F32.wireOp",EDGE,"E120.2.4.0")])]})});
            var Q32;
            Q32=makeQuery(id+"F33.boolean.opBoolean","COPY",EDGE,{"derivedFrom":makeQuery(id+"F33.opExtrude","SWEPT_EDGE",EDGE,{"disambiguationData":[OSD([sQuery(id+"F32.wireOp",EDGE,"E116"),sQuery(id+"F32.wireOp",EDGE,"E120.6.3.0")])]})});
            var Q33;
            Q33=makeQuery(id+"F33.boolean.opBoolean","COPY",EDGE,{"derivedFrom":makeQuery(id+"F33.opExtrude","SWEPT_EDGE",EDGE,{"disambiguationData":[OSD([sQuery(id+"F32.wireOp",EDGE,"E115"),sQuery(id+"F32.wireOp",EDGE,"E120.6.3.0")])]})});
            var Q34;
            Q34=makeQuery(id+"F33.boolean.opBoolean","COPY",EDGE,{"derivedFrom":makeQuery(id+"F33.opExtrude","SWEPT_EDGE",EDGE,{"disambiguationData":[OSD([sQuery(id+"F32.wireOp",EDGE,"E115"),sQuery(id+"F32.wireOp",EDGE,"E120.2.3.0")])]})});
            var Q35;
            Q35=makeQuery(id+"F33.boolean.opBoolean","COPY",EDGE,{"derivedFrom":makeQuery(id+"F33.opExtrude","SWEPT_EDGE",EDGE,{"disambiguationData":[OSD([sQuery(id+"F32.wireOp",EDGE,"E116"),sQuery(id+"F32.wireOp",EDGE,"E120.2.3.0")])]})});
            fillet(context, id + "F34", {"entities" : qUnion([Q0, Q1, Q2, Q3, Q4, Q5, Q6, Q7, Q8, Q9, Q10, Q11, Q12, Q13, Q14, Q15, Q16, Q17, Q18, Q19, Q20, Q21, Q22, Q23, Q24, Q25, Q26, Q27, Q28, Q29, Q30, Q31, Q32, Q33, Q34, Q35]), "radius" : getVariable(context, 'duron_thin'), "tangentPropagation" : true, "allowEdgeOverflow" : false});
        }
        {
            var Q0;
            Q0=makeQuery(id+"F11.opExtrude","SWEPT_EDGE",EDGE,{"disambiguationData":[OSD([sQuery(id+"F10.wireOp",EDGE,"E15.bottom"),sQuery(id+"F10.wireOp",EDGE,"E15.right")])]});
            var Q1;
            Q1=makeQuery(id+"F11.opExtrude","SWEPT_EDGE",EDGE,{"disambiguationData":[OSD([sQuery(id+"F10.wireOp",EDGE,"E15.top"),sQuery(id+"F10.wireOp",EDGE,"E15.right")])]});
            var Q2;
            Q2=makeQuery(id+"F11.opExtrude","SWEPT_EDGE",EDGE,{"disambiguationData":[OSD([sQuery(id+"F10.wireOp",EDGE,"E15.bottom"),sQuery(id+"F10.wireOp",EDGE,"E15.left")])]});
            var Q3;
            Q3=makeQuery(id+"F11.opExtrude","SWEPT_EDGE",EDGE,{"disambiguationData":[OSD([sQuery(id+"F10.wireOp",EDGE,"E15.top"),sQuery(id+"F10.wireOp",EDGE,"E15.left")])]});
            fillet(context, id + "F35", {"entities" : qUnion([Q0, Q1, Q2, Q3]), "radius" : 9.52 * mm, "tangentPropagation" : true, "allowEdgeOverflow" : false});
        }
        {
            var Q0;
            Q0=makeQuery(id+"F11.opExtrude","CAP_FACE",FACE,{"disambiguationData":[OSD([sQuery(id+"F10.wireOp",EDGE,"E15.bottom"),sQuery(id+"F10.wireOp",EDGE,"E15.top"),sQuery(id+"F10.wireOp",EDGE,"E15.left"),sQuery(id+"F10.wireOp",EDGE,"E15.right")])],"isStart":true});
            var sketch = newSketch(context, id + "F36", { "sketchPlane" : qUnion([Q0])});
            skPoint(sketch, "E125", {"position": v(-117.53, 60.53) * mm});
            skPoint(sketch, "E126", {"position": v(120.53, 60.53) * mm});
            skPoint(sketch, "E127", {"position": v(120.53, -6.15) * mm});
            skPoint(sketch, "E128", {"position": v(-117.53, -6.15) * mm});
            skSolve(sketch);
        }
        {
            var Q0;
            Q0=sQuery(id+"F36.wireOp",VERTEX,"E125");
            var Q1;
            Q1=sQuery(id+"F36.wireOp",VERTEX,"E128");
            var Q2;
            Q2=sQuery(id+"F36.wireOp",VERTEX,"E126");
            var Q3;
            Q3=sQuery(id+"F36.wireOp",VERTEX,"E127");
            var Q4;
            Q4=makeQuery(id+"F11.opExtrude","SWEPT_BODY",BODY,{"disambiguationData":[OSD([sQuery(id+"F10.wireOp",EDGE,"E15.bottom"),sQuery(id+"F10.wireOp",EDGE,"E15.top"),sQuery(id+"F10.wireOp",EDGE,"E15.left"),sQuery(id+"F10.wireOp",EDGE,"E15.right")])]});
            hole(context, id + "F37", {"style" : HoleStyle.SIMPLE, "holeDiameter" : 4.76 * mm, "endStyle" : HoleEndStyle.THROUGH, "locations" : qUnion([Q0, Q1, Q2, Q3]), "scope" : qUnion([Q4])});
        }
        {
            var Q0;
            Q0=makeQuery(id+"F24.opExtrude","SWEPT_EDGE",EDGE,{"disambiguationData":[OSD([sQuery(id+"F23.wireOp",EDGE,"E81.0"),sQuery(id+"F23.wireOp",EDGE,"E85")])]});
            var Q1;
            Q1=makeQuery(id+"F13.opExtrude","SWEPT_EDGE",EDGE,{"disambiguationData":[OSD([sQuery(id+"F12.wireOp",EDGE,"E18"),sQuery(id+"F12.wireOp",EDGE,"E20")])]});
            var Q2;
            Q2=makeQuery(id+"F13.opExtrude","SWEPT_EDGE",EDGE,{"disambiguationData":[OSD([sQuery(id+"F12.wireOp",EDGE,"E18"),sQuery(id+"F12.wireOp",EDGE,"E19")])]});
            var Q3;
            Q3=makeQuery(id+"F26.opExtrude","SWEPT_EDGE",EDGE,{"disambiguationData":[OSD([sQuery(id+"F25.wireOp",EDGE,"E94.0"),sQuery(id+"F25.wireOp",EDGE,"E96.0")])]});
            var Q4;
            Q4=makeQuery(id+"F26.opExtrude","SWEPT_EDGE",EDGE,{"disambiguationData":[OSD([sQuery(id+"F25.wireOp",EDGE,"E93.0"),sQuery(id+"F25.wireOp",EDGE,"E94.0")])]});
            var Q5;
            Q5=makeQuery(id+"F13.opExtrude","SWEPT_EDGE",EDGE,{"disambiguationData":[OSD([sQuery(id+"F12.wireOp",EDGE,"E19"),sQuery(id+"F12.wireOp",EDGE,"E22")])]});
            var Q6;
            Q6=makeQuery(id+"F24.opExtrude","SWEPT_EDGE",EDGE,{"disambiguationData":[OSD([sQuery(id+"F23.wireOp",EDGE,"E81.0"),sQuery(id+"F23.wireOp",EDGE,"E82.0")])]});
            var Q7;
            Q7=makeQuery(id+"F13.opExtrude","SWEPT_EDGE",EDGE,{"disambiguationData":[OSD([sQuery(id+"F12.wireOp",EDGE,"E20"),sQuery(id+"F12.wireOp",EDGE,"E21")])]});
            fillet(context, id + "F38", {"entities" : qUnion([Q0, Q1, Q2, Q3, Q4, Q5, Q6, Q7]), "radius" : 2.54 * mm, "tangentPropagation" : true, "allowEdgeOverflow" : false});
        }
    });
